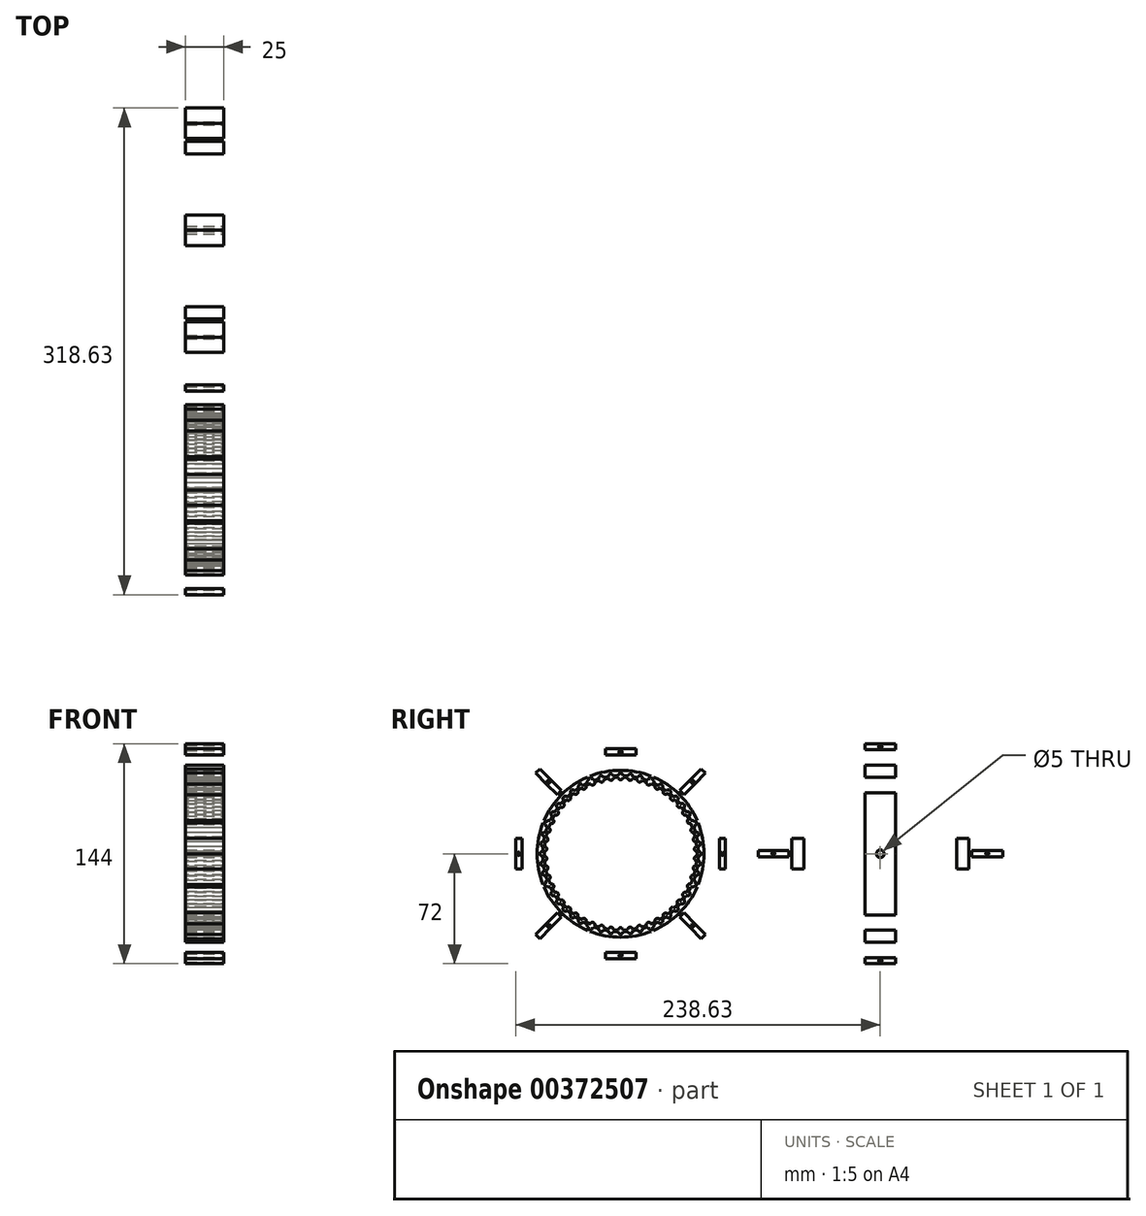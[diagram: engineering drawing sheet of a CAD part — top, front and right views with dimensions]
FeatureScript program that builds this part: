
annotation { "Feature Type Name" : "Feature", "Feature Type Description" : "" }
export const myFeature = defineFeature(function(context is Context, id is Id, definition is map)
    precondition{}
    {
        {
            var Q0;
            Q0=qCreatedBy(makeId("Right.planeOp"),FACE);
            var sketch = newSketch(context, id + "F0", { "sketchPlane" : qUnion([Q0])});
            skLineSegment(sketch, "E0", {"start": v(0, 0) * mm, "end": v(0, 50) * mm, "construction": true});
            skArc(sketch, "E1", {"start": v(3.14, 49.9) * mm, "mid": v(1.57, 49.98) * mm, "end": v(0, 50) * mm});
            skArc(sketch, "E2", {"start": v(-3.14, 49.9) * mm, "mid": v(-1.57, 49.98) * mm, "end": v(0, 50) * mm, "construction": true});
            skArc(sketch, "E3", {"start": v(0, 50) * mm, "mid": v(-1.52, 48.4) * mm, "end": v(-3.14, 49.9) * mm});
            skPoint(sketch, "E3.centerSnap0", {"position": v(-1.57, 49.98) * mm});
            skLineSegment(sketch, "E4", {"start": v(-3.14, 49.9) * mm, "end": v(0, 0) * mm, "construction": true});
            skLineSegment(sketch, "E5", {"start": v(3.14, 49.9) * mm, "end": v(0, 0) * mm, "construction": true});
            skArc(sketch, "E6.1.0", {"start": v(-3.14, 49.9) * mm, "mid": v(-4.7, 49.78) * mm, "end": v(-6.27, 49.6) * mm});
            skArc(sketch, "E6.1.1", {"start": v(-6.27, 49.6) * mm, "mid": v(-7.58, 47.83) * mm, "end": v(-9.37, 49.11) * mm});
            skArc(sketch, "E6.2.0", {"start": v(-9.37, 49.11) * mm, "mid": v(-10.9, 48.8) * mm, "end": v(-12.43, 48.43) * mm});
            skArc(sketch, "E6.2.1", {"start": v(-12.43, 48.43) * mm, "mid": v(-13.51, 46.5) * mm, "end": v(-15.45, 47.55) * mm});
            skArc(sketch, "E7.3.3.0", {"start": v(-15.45, 47.55) * mm, "mid": v(-16.94, 47.04) * mm, "end": v(-18.4, 46.49) * mm});
            skArc(sketch, "E7.4.3.0", {"start": v(-18.4, 46.49) * mm, "mid": v(-19.23, 44.45) * mm, "end": v(-21.29, 45.24) * mm});
            skArc(sketch, "E7.3.4.0", {"start": v(-21.29, 45.24) * mm, "mid": v(-22.7, 44.55) * mm, "end": v(-24.09, 43.82) * mm});
            skArc(sketch, "E7.4.4.0", {"start": v(-24.09, 43.82) * mm, "mid": v(-24.65, 41.69) * mm, "end": v(-26.8, 42.22) * mm});
            skArc(sketch, "E7.3.5.0", {"start": v(-26.8, 42.22) * mm, "mid": v(-28.1, 41.35) * mm, "end": v(-29.39, 40.45) * mm});
            skArc(sketch, "E7.4.5.0", {"start": v(-29.39, 40.45) * mm, "mid": v(-29.68, 38.27) * mm, "end": v(-31.87, 38.53) * mm});
            skArc(sketch, "E7.3.6.0", {"start": v(-31.87, 38.53) * mm, "mid": v(-33.07, 37.5) * mm, "end": v(-34.23, 36.45) * mm});
            skArc(sketch, "E7.4.6.0", {"start": v(-34.23, 36.45) * mm, "mid": v(-34.24, 34.24) * mm, "end": v(-36.45, 34.23) * mm});
            skArc(sketch, "E7.3.7.0", {"start": v(-36.45, 34.23) * mm, "mid": v(-37.5, 33.07) * mm, "end": v(-38.53, 31.87) * mm});
            skArc(sketch, "E7.4.7.0", {"start": v(-38.53, 31.87) * mm, "mid": v(-38.27, 29.68) * mm, "end": v(-40.45, 29.39) * mm});
            skArc(sketch, "E7.3.8.0", {"start": v(-40.45, 29.39) * mm, "mid": v(-41.35, 28.1) * mm, "end": v(-42.22, 26.8) * mm});
            skArc(sketch, "E7.4.8.0", {"start": v(-42.22, 26.8) * mm, "mid": v(-41.69, 24.65) * mm, "end": v(-43.82, 24.09) * mm});
            skArc(sketch, "E7.3.9.0", {"start": v(-43.82, 24.09) * mm, "mid": v(-44.55, 22.7) * mm, "end": v(-45.24, 21.29) * mm});
            skArc(sketch, "E7.4.9.0", {"start": v(-45.24, 21.29) * mm, "mid": v(-44.45, 19.23) * mm, "end": v(-46.49, 18.4) * mm});
            skArc(sketch, "E7.3.10.0", {"start": v(-46.49, 18.4) * mm, "mid": v(-47.04, 16.94) * mm, "end": v(-47.55, 15.45) * mm});
            skArc(sketch, "E7.4.10.0", {"start": v(-47.55, 15.45) * mm, "mid": v(-46.5, 13.51) * mm, "end": v(-48.43, 12.43) * mm});
            skArc(sketch, "E7.3.11.0", {"start": v(-48.43, 12.43) * mm, "mid": v(-48.8, 10.9) * mm, "end": v(-49.11, 9.37) * mm});
            skArc(sketch, "E7.4.11.0", {"start": v(-49.11, 9.37) * mm, "mid": v(-47.83, 7.58) * mm, "end": v(-49.6, 6.27) * mm});
            skArc(sketch, "E7.3.12.0", {"start": v(-49.6, 6.27) * mm, "mid": v(-49.78, 4.7) * mm, "end": v(-49.9, 3.14) * mm});
            skArc(sketch, "E7.4.12.0", {"start": v(-49.9, 3.14) * mm, "mid": v(-48.4, 1.52) * mm, "end": v(-50, 0) * mm});
            skArc(sketch, "E7.3.13.0", {"start": v(-50, 0) * mm, "mid": v(-49.98, -1.57) * mm, "end": v(-49.9, -3.14) * mm});
            skArc(sketch, "E7.4.13.0", {"start": v(-49.9, -3.14) * mm, "mid": v(-48.21, -4.56) * mm, "end": v(-49.6, -6.27) * mm});
            skArc(sketch, "E7.3.14.0", {"start": v(-49.6, -6.27) * mm, "mid": v(-49.38, -7.82) * mm, "end": v(-49.11, -9.37) * mm});
            skArc(sketch, "E7.4.14.0", {"start": v(-49.11, -9.37) * mm, "mid": v(-47.26, -10.56) * mm, "end": v(-48.43, -12.43) * mm});
            skArc(sketch, "E7.3.15.0", {"start": v(-48.43, -12.43) * mm, "mid": v(-48.01, -13.95) * mm, "end": v(-47.55, -15.45) * mm});
            skArc(sketch, "E7.4.15.0", {"start": v(-47.55, -15.45) * mm, "mid": v(-45.57, -16.4) * mm, "end": v(-46.49, -18.4) * mm});
            skArc(sketch, "E7.3.16.0", {"start": v(-46.49, -18.4) * mm, "mid": v(-45.89, -19.86) * mm, "end": v(-45.24, -21.29) * mm});
            skArc(sketch, "E7.4.16.0", {"start": v(-45.24, -21.29) * mm, "mid": v(-43.15, -21.99) * mm, "end": v(-43.82, -24.09) * mm});
            skArc(sketch, "E7.3.17.0", {"start": v(-43.82, -24.09) * mm, "mid": v(-43.04, -25.45) * mm, "end": v(-42.22, -26.8) * mm});
            skArc(sketch, "E7.4.17.0", {"start": v(-42.22, -26.8) * mm, "mid": v(-40.05, -27.22) * mm, "end": v(-40.45, -29.39) * mm});
            skArc(sketch, "E7.3.18.0", {"start": v(-40.45, -29.39) * mm, "mid": v(-39.5, -30.65) * mm, "end": v(-38.53, -31.87) * mm});
            skArc(sketch, "E7.4.18.0", {"start": v(-38.53, -31.87) * mm, "mid": v(-36.33, -32.03) * mm, "end": v(-36.45, -34.23) * mm});
            skArc(sketch, "E7.3.19.0", {"start": v(-36.45, -34.23) * mm, "mid": v(-35.36, -35.36) * mm, "end": v(-34.23, -36.45) * mm});
            skArc(sketch, "E7.4.19.0", {"start": v(-34.23, -36.45) * mm, "mid": v(-32.03, -36.33) * mm, "end": v(-31.87, -38.53) * mm});
            skArc(sketch, "E7.3.20.0", {"start": v(-31.87, -38.53) * mm, "mid": v(-30.65, -39.5) * mm, "end": v(-29.39, -40.45) * mm});
            skArc(sketch, "E7.4.20.0", {"start": v(-29.39, -40.45) * mm, "mid": v(-27.22, -40.05) * mm, "end": v(-26.8, -42.22) * mm});
            skArc(sketch, "E7.3.21.0", {"start": v(-26.8, -42.22) * mm, "mid": v(-25.45, -43.04) * mm, "end": v(-24.09, -43.82) * mm});
            skArc(sketch, "E7.4.21.0", {"start": v(-24.09, -43.82) * mm, "mid": v(-21.99, -43.15) * mm, "end": v(-21.29, -45.24) * mm});
            skArc(sketch, "E7.3.22.0", {"start": v(-21.29, -45.24) * mm, "mid": v(-19.86, -45.89) * mm, "end": v(-18.4, -46.49) * mm});
            skArc(sketch, "E7.4.22.0", {"start": v(-18.4, -46.49) * mm, "mid": v(-16.4, -45.57) * mm, "end": v(-15.45, -47.55) * mm});
            skArc(sketch, "E7.3.23.0", {"start": v(-15.45, -47.55) * mm, "mid": v(-13.95, -48.01) * mm, "end": v(-12.43, -48.43) * mm});
            skArc(sketch, "E7.4.23.0", {"start": v(-12.43, -48.43) * mm, "mid": v(-10.56, -47.26) * mm, "end": v(-9.37, -49.11) * mm});
            skArc(sketch, "E7.3.24.0", {"start": v(-9.37, -49.11) * mm, "mid": v(-7.82, -49.38) * mm, "end": v(-6.27, -49.6) * mm});
            skArc(sketch, "E7.4.24.0", {"start": v(-6.27, -49.6) * mm, "mid": v(-4.56, -48.21) * mm, "end": v(-3.14, -49.9) * mm});
            skArc(sketch, "E7.3.25.0", {"start": v(-3.14, -49.9) * mm, "mid": v(-1.57, -49.98) * mm, "end": v(0, -50) * mm});
            skArc(sketch, "E7.4.25.0", {"start": v(0, -50) * mm, "mid": v(1.52, -48.4) * mm, "end": v(3.14, -49.9) * mm});
            skArc(sketch, "E7.3.26.0", {"start": v(3.14, -49.9) * mm, "mid": v(4.7, -49.78) * mm, "end": v(6.27, -49.6) * mm});
            skArc(sketch, "E7.4.26.0", {"start": v(6.27, -49.6) * mm, "mid": v(7.58, -47.83) * mm, "end": v(9.37, -49.11) * mm});
            skArc(sketch, "E7.3.27.0", {"start": v(9.37, -49.11) * mm, "mid": v(10.9, -48.8) * mm, "end": v(12.43, -48.43) * mm});
            skArc(sketch, "E7.4.27.0", {"start": v(12.43, -48.43) * mm, "mid": v(13.51, -46.5) * mm, "end": v(15.45, -47.55) * mm});
            skArc(sketch, "E7.3.28.0", {"start": v(15.45, -47.55) * mm, "mid": v(16.94, -47.04) * mm, "end": v(18.4, -46.49) * mm});
            skArc(sketch, "E7.4.28.0", {"start": v(18.4, -46.49) * mm, "mid": v(19.23, -44.45) * mm, "end": v(21.29, -45.24) * mm});
            skArc(sketch, "E7.3.29.0", {"start": v(21.29, -45.24) * mm, "mid": v(22.7, -44.55) * mm, "end": v(24.09, -43.82) * mm});
            skArc(sketch, "E7.4.29.0", {"start": v(24.09, -43.82) * mm, "mid": v(24.65, -41.69) * mm, "end": v(26.8, -42.22) * mm});
            skArc(sketch, "E7.3.30.0", {"start": v(26.8, -42.22) * mm, "mid": v(28.1, -41.35) * mm, "end": v(29.39, -40.45) * mm});
            skArc(sketch, "E7.4.30.0", {"start": v(29.39, -40.45) * mm, "mid": v(29.68, -38.27) * mm, "end": v(31.87, -38.53) * mm});
            skArc(sketch, "E7.3.31.0", {"start": v(31.87, -38.53) * mm, "mid": v(33.07, -37.5) * mm, "end": v(34.23, -36.45) * mm});
            skArc(sketch, "E7.4.31.0", {"start": v(34.23, -36.45) * mm, "mid": v(34.24, -34.24) * mm, "end": v(36.45, -34.23) * mm});
            skArc(sketch, "E7.3.32.0", {"start": v(36.45, -34.23) * mm, "mid": v(37.5, -33.07) * mm, "end": v(38.53, -31.87) * mm});
            skArc(sketch, "E7.4.32.0", {"start": v(38.53, -31.87) * mm, "mid": v(38.27, -29.68) * mm, "end": v(40.45, -29.39) * mm});
            skArc(sketch, "E7.3.33.0", {"start": v(40.45, -29.39) * mm, "mid": v(41.35, -28.1) * mm, "end": v(42.22, -26.8) * mm});
            skArc(sketch, "E7.4.33.0", {"start": v(42.22, -26.8) * mm, "mid": v(41.69, -24.65) * mm, "end": v(43.82, -24.09) * mm});
            skArc(sketch, "E7.3.34.0", {"start": v(43.82, -24.09) * mm, "mid": v(44.55, -22.7) * mm, "end": v(45.24, -21.29) * mm});
            skArc(sketch, "E7.4.34.0", {"start": v(45.24, -21.29) * mm, "mid": v(44.45, -19.23) * mm, "end": v(46.49, -18.4) * mm});
            skArc(sketch, "E7.3.35.0", {"start": v(46.49, -18.4) * mm, "mid": v(47.04, -16.94) * mm, "end": v(47.55, -15.45) * mm});
            skArc(sketch, "E7.4.35.0", {"start": v(47.55, -15.45) * mm, "mid": v(46.5, -13.51) * mm, "end": v(48.43, -12.43) * mm});
            skArc(sketch, "E7.3.36.0", {"start": v(48.43, -12.43) * mm, "mid": v(48.8, -10.9) * mm, "end": v(49.11, -9.37) * mm});
            skArc(sketch, "E7.4.36.0", {"start": v(49.11, -9.37) * mm, "mid": v(47.83, -7.58) * mm, "end": v(49.6, -6.27) * mm});
            skArc(sketch, "E7.3.37.0", {"start": v(49.6, -6.27) * mm, "mid": v(49.78, -4.7) * mm, "end": v(49.9, -3.14) * mm});
            skArc(sketch, "E7.4.37.0", {"start": v(49.9, -3.14) * mm, "mid": v(48.4, -1.52) * mm, "end": v(50, 0) * mm});
            skArc(sketch, "E7.3.38.0", {"start": v(50, 0) * mm, "mid": v(49.98, 1.57) * mm, "end": v(49.9, 3.14) * mm});
            skArc(sketch, "E7.4.38.0", {"start": v(49.9, 3.14) * mm, "mid": v(48.21, 4.56) * mm, "end": v(49.6, 6.27) * mm});
            skArc(sketch, "E7.3.39.0", {"start": v(49.6, 6.27) * mm, "mid": v(49.38, 7.82) * mm, "end": v(49.11, 9.37) * mm});
            skArc(sketch, "E7.4.39.0", {"start": v(49.11, 9.37) * mm, "mid": v(47.26, 10.56) * mm, "end": v(48.43, 12.43) * mm});
            skArc(sketch, "E7.3.40.0", {"start": v(48.43, 12.43) * mm, "mid": v(48.01, 13.95) * mm, "end": v(47.55, 15.45) * mm});
            skArc(sketch, "E7.4.40.0", {"start": v(47.55, 15.45) * mm, "mid": v(45.57, 16.4) * mm, "end": v(46.49, 18.4) * mm});
            skArc(sketch, "E7.3.41.0", {"start": v(46.49, 18.4) * mm, "mid": v(45.89, 19.86) * mm, "end": v(45.24, 21.29) * mm});
            skArc(sketch, "E7.4.41.0", {"start": v(45.24, 21.29) * mm, "mid": v(43.15, 21.99) * mm, "end": v(43.82, 24.09) * mm});
            skArc(sketch, "E7.3.42.0", {"start": v(43.82, 24.09) * mm, "mid": v(43.04, 25.45) * mm, "end": v(42.22, 26.8) * mm});
            skArc(sketch, "E7.4.42.0", {"start": v(42.22, 26.8) * mm, "mid": v(40.05, 27.22) * mm, "end": v(40.45, 29.39) * mm});
            skArc(sketch, "E7.3.43.0", {"start": v(40.45, 29.39) * mm, "mid": v(39.5, 30.65) * mm, "end": v(38.53, 31.87) * mm});
            skArc(sketch, "E7.4.43.0", {"start": v(38.53, 31.87) * mm, "mid": v(36.33, 32.03) * mm, "end": v(36.45, 34.23) * mm});
            skArc(sketch, "E7.3.44.0", {"start": v(36.45, 34.23) * mm, "mid": v(35.36, 35.36) * mm, "end": v(34.23, 36.45) * mm});
            skArc(sketch, "E7.4.44.0", {"start": v(34.23, 36.45) * mm, "mid": v(32.03, 36.33) * mm, "end": v(31.87, 38.53) * mm});
            skArc(sketch, "E7.3.45.0", {"start": v(31.87, 38.53) * mm, "mid": v(30.65, 39.5) * mm, "end": v(29.39, 40.45) * mm});
            skArc(sketch, "E7.4.45.0", {"start": v(29.39, 40.45) * mm, "mid": v(27.22, 40.05) * mm, "end": v(26.8, 42.22) * mm});
            skArc(sketch, "E7.3.46.0", {"start": v(26.8, 42.22) * mm, "mid": v(25.45, 43.04) * mm, "end": v(24.09, 43.82) * mm});
            skArc(sketch, "E7.4.46.0", {"start": v(24.09, 43.82) * mm, "mid": v(21.99, 43.15) * mm, "end": v(21.29, 45.24) * mm});
            skArc(sketch, "E7.3.47.0", {"start": v(21.29, 45.24) * mm, "mid": v(19.86, 45.89) * mm, "end": v(18.4, 46.49) * mm});
            skArc(sketch, "E7.4.47.0", {"start": v(18.4, 46.49) * mm, "mid": v(16.4, 45.57) * mm, "end": v(15.45, 47.55) * mm});
            skArc(sketch, "E7.3.48.0", {"start": v(15.45, 47.55) * mm, "mid": v(13.95, 48.01) * mm, "end": v(12.43, 48.43) * mm});
            skArc(sketch, "E7.4.48.0", {"start": v(12.43, 48.43) * mm, "mid": v(10.56, 47.26) * mm, "end": v(9.37, 49.11) * mm});
            skArc(sketch, "E7.3.49.0", {"start": v(9.37, 49.11) * mm, "mid": v(7.82, 49.38) * mm, "end": v(6.27, 49.6) * mm});
            skArc(sketch, "E7.4.49.0", {"start": v(6.27, 49.6) * mm, "mid": v(4.56, 48.21) * mm, "end": v(3.14, 49.9) * mm});
            skArc(sketch, "E8", {"start": v(0, 50) * mm, "mid": v(1.57, 49.98) * mm, "end": v(3.14, 49.9) * mm, "construction": true});
            skLineSegment(sketch, "E9", {"start": v(0, 25) * mm, "end": v(-1.57, 25) * mm, "construction": true});
            skLineSegment(sketch, "E10", {"start": v(0, 25) * mm, "end": v(1.57, 25) * mm, "construction": true});
            skSolve(sketch);
        }
        {
            var Q0;
            Q0 = qSketchRegion(id + "F0", true);
            extrude(context, id + "F1", {"entities" : qUnion([Q0]), "depth" : 25 * mm});
        }
        {
            var Q0;
            Q0=makeQuery(id+"F1.opExtrude","CAP_FACE",FACE,{"disambiguationData":[OSD([sQuery(id+"F0.wireOp",EDGE,"E1"),sQuery(id+"F0.wireOp",EDGE,"E3"),sQuery(id+"F0.wireOp",EDGE,"E6.1.0"),sQuery(id+"F0.wireOp",EDGE,"E6.1.1"),sQuery(id+"F0.wireOp",EDGE,"E6.2.0"),sQuery(id+"F0.wireOp",EDGE,"E6.2.1"),sQuery(id+"F0.wireOp",EDGE,"E7.3.3.0"),sQuery(id+"F0.wireOp",EDGE,"E7.4.3.0"),sQuery(id+"F0.wireOp",EDGE,"E7.3.4.0"),sQuery(id+"F0.wireOp",EDGE,"E7.4.4.0"),sQuery(id+"F0.wireOp",EDGE,"E7.3.5.0"),sQuery(id+"F0.wireOp",EDGE,"E7.4.5.0"),sQuery(id+"F0.wireOp",EDGE,"E7.3.6.0"),sQuery(id+"F0.wireOp",EDGE,"E7.4.6.0"),sQuery(id+"F0.wireOp",EDGE,"E7.3.7.0"),sQuery(id+"F0.wireOp",EDGE,"E7.4.7.0"),sQuery(id+"F0.wireOp",EDGE,"E7.3.8.0"),sQuery(id+"F0.wireOp",EDGE,"E7.4.8.0"),sQuery(id+"F0.wireOp",EDGE,"E7.3.9.0"),sQuery(id+"F0.wireOp",EDGE,"E7.4.9.0"),sQuery(id+"F0.wireOp",EDGE,"E7.3.10.0"),sQuery(id+"F0.wireOp",EDGE,"E7.4.10.0"),sQuery(id+"F0.wireOp",EDGE,"E7.3.11.0"),sQuery(id+"F0.wireOp",EDGE,"E7.4.11.0"),sQuery(id+"F0.wireOp",EDGE,"E7.3.12.0"),sQuery(id+"F0.wireOp",EDGE,"E7.4.12.0"),sQuery(id+"F0.wireOp",EDGE,"E7.3.13.0"),sQuery(id+"F0.wireOp",EDGE,"E7.4.13.0"),sQuery(id+"F0.wireOp",EDGE,"E7.3.14.0"),sQuery(id+"F0.wireOp",EDGE,"E7.4.14.0"),sQuery(id+"F0.wireOp",EDGE,"E7.3.15.0"),sQuery(id+"F0.wireOp",EDGE,"E7.4.15.0"),sQuery(id+"F0.wireOp",EDGE,"E7.3.16.0"),sQuery(id+"F0.wireOp",EDGE,"E7.4.16.0"),sQuery(id+"F0.wireOp",EDGE,"E7.3.17.0"),sQuery(id+"F0.wireOp",EDGE,"E7.4.17.0"),sQuery(id+"F0.wireOp",EDGE,"E7.3.18.0"),sQuery(id+"F0.wireOp",EDGE,"E7.4.18.0"),sQuery(id+"F0.wireOp",EDGE,"E7.3.19.0"),sQuery(id+"F0.wireOp",EDGE,"E7.4.19.0"),sQuery(id+"F0.wireOp",EDGE,"E7.3.20.0"),sQuery(id+"F0.wireOp",EDGE,"E7.4.20.0"),sQuery(id+"F0.wireOp",EDGE,"E7.3.21.0"),sQuery(id+"F0.wireOp",EDGE,"E7.4.21.0"),sQuery(id+"F0.wireOp",EDGE,"E7.3.22.0"),sQuery(id+"F0.wireOp",EDGE,"E7.4.22.0"),sQuery(id+"F0.wireOp",EDGE,"E7.3.23.0"),sQuery(id+"F0.wireOp",EDGE,"E7.4.23.0"),sQuery(id+"F0.wireOp",EDGE,"E7.3.24.0"),sQuery(id+"F0.wireOp",EDGE,"E7.4.24.0"),sQuery(id+"F0.wireOp",EDGE,"E7.3.25.0"),sQuery(id+"F0.wireOp",EDGE,"E7.4.25.0"),sQuery(id+"F0.wireOp",EDGE,"E7.3.26.0"),sQuery(id+"F0.wireOp",EDGE,"E7.4.26.0"),sQuery(id+"F0.wireOp",EDGE,"E7.3.27.0"),sQuery(id+"F0.wireOp",EDGE,"E7.4.27.0"),sQuery(id+"F0.wireOp",EDGE,"E7.3.28.0"),sQuery(id+"F0.wireOp",EDGE,"E7.4.28.0"),sQuery(id+"F0.wireOp",EDGE,"E7.3.29.0"),sQuery(id+"F0.wireOp",EDGE,"E7.4.29.0"),sQuery(id+"F0.wireOp",EDGE,"E7.3.30.0"),sQuery(id+"F0.wireOp",EDGE,"E7.4.30.0"),sQuery(id+"F0.wireOp",EDGE,"E7.3.31.0"),sQuery(id+"F0.wireOp",EDGE,"E7.4.31.0"),sQuery(id+"F0.wireOp",EDGE,"E7.3.32.0"),sQuery(id+"F0.wireOp",EDGE,"E7.4.32.0"),sQuery(id+"F0.wireOp",EDGE,"E7.3.33.0"),sQuery(id+"F0.wireOp",EDGE,"E7.4.33.0"),sQuery(id+"F0.wireOp",EDGE,"E7.3.34.0"),sQuery(id+"F0.wireOp",EDGE,"E7.4.34.0"),sQuery(id+"F0.wireOp",EDGE,"E7.3.35.0"),sQuery(id+"F0.wireOp",EDGE,"E7.4.35.0"),sQuery(id+"F0.wireOp",EDGE,"E7.3.36.0"),sQuery(id+"F0.wireOp",EDGE,"E7.4.36.0"),sQuery(id+"F0.wireOp",EDGE,"E7.3.37.0"),sQuery(id+"F0.wireOp",EDGE,"E7.4.37.0"),sQuery(id+"F0.wireOp",EDGE,"E7.3.38.0"),sQuery(id+"F0.wireOp",EDGE,"E7.4.38.0"),sQuery(id+"F0.wireOp",EDGE,"E7.3.39.0"),sQuery(id+"F0.wireOp",EDGE,"E7.4.39.0"),sQuery(id+"F0.wireOp",EDGE,"E7.3.40.0"),sQuery(id+"F0.wireOp",EDGE,"E7.4.40.0"),sQuery(id+"F0.wireOp",EDGE,"E7.3.41.0"),sQuery(id+"F0.wireOp",EDGE,"E7.4.41.0"),sQuery(id+"F0.wireOp",EDGE,"E7.3.42.0"),sQuery(id+"F0.wireOp",EDGE,"E7.4.42.0"),sQuery(id+"F0.wireOp",EDGE,"E7.3.43.0"),sQuery(id+"F0.wireOp",EDGE,"E7.4.43.0"),sQuery(id+"F0.wireOp",EDGE,"E7.3.44.0"),sQuery(id+"F0.wireOp",EDGE,"E7.4.44.0"),sQuery(id+"F0.wireOp",EDGE,"E7.3.45.0"),sQuery(id+"F0.wireOp",EDGE,"E7.4.45.0"),sQuery(id+"F0.wireOp",EDGE,"E7.3.46.0"),sQuery(id+"F0.wireOp",EDGE,"E7.4.46.0"),sQuery(id+"F0.wireOp",EDGE,"E7.3.47.0"),sQuery(id+"F0.wireOp",EDGE,"E7.4.47.0"),sQuery(id+"F0.wireOp",EDGE,"E7.3.48.0"),sQuery(id+"F0.wireOp",EDGE,"E7.4.48.0"),sQuery(id+"F0.wireOp",EDGE,"E7.3.49.0"),sQuery(id+"F0.wireOp",EDGE,"E7.4.49.0")])],"isStart":false});
            var sketch = newSketch(context, id + "F2", { "sketchPlane" : qUnion([Q0])});
            skCircle(sketch, "E11", {"center": v(0, 0) * mm, "radius": 56.89 * mm, "construction": true});
            skSolve(sketch);
        }
        {
            var Q0;
            Q0=makeQuery(id+"F1.opExtrude","SWEPT_BODY",BODY,{"disambiguationData":[OSD([sQuery(id+"F0.wireOp",EDGE,"E1"),sQuery(id+"F0.wireOp",EDGE,"E3"),sQuery(id+"F0.wireOp",EDGE,"E6.1.0"),sQuery(id+"F0.wireOp",EDGE,"E6.1.1"),sQuery(id+"F0.wireOp",EDGE,"E6.2.0"),sQuery(id+"F0.wireOp",EDGE,"E6.2.1"),sQuery(id+"F0.wireOp",EDGE,"E7.3.3.0"),sQuery(id+"F0.wireOp",EDGE,"E7.4.3.0"),sQuery(id+"F0.wireOp",EDGE,"E7.3.4.0"),sQuery(id+"F0.wireOp",EDGE,"E7.4.4.0"),sQuery(id+"F0.wireOp",EDGE,"E7.3.5.0"),sQuery(id+"F0.wireOp",EDGE,"E7.4.5.0"),sQuery(id+"F0.wireOp",EDGE,"E7.3.6.0"),sQuery(id+"F0.wireOp",EDGE,"E7.4.6.0"),sQuery(id+"F0.wireOp",EDGE,"E7.3.7.0"),sQuery(id+"F0.wireOp",EDGE,"E7.4.7.0"),sQuery(id+"F0.wireOp",EDGE,"E7.3.8.0"),sQuery(id+"F0.wireOp",EDGE,"E7.4.8.0"),sQuery(id+"F0.wireOp",EDGE,"E7.3.9.0"),sQuery(id+"F0.wireOp",EDGE,"E7.4.9.0"),sQuery(id+"F0.wireOp",EDGE,"E7.3.10.0"),sQuery(id+"F0.wireOp",EDGE,"E7.4.10.0"),sQuery(id+"F0.wireOp",EDGE,"E7.3.11.0"),sQuery(id+"F0.wireOp",EDGE,"E7.4.11.0"),sQuery(id+"F0.wireOp",EDGE,"E7.3.12.0"),sQuery(id+"F0.wireOp",EDGE,"E7.4.12.0"),sQuery(id+"F0.wireOp",EDGE,"E7.3.13.0"),sQuery(id+"F0.wireOp",EDGE,"E7.4.13.0"),sQuery(id+"F0.wireOp",EDGE,"E7.3.14.0"),sQuery(id+"F0.wireOp",EDGE,"E7.4.14.0"),sQuery(id+"F0.wireOp",EDGE,"E7.3.15.0"),sQuery(id+"F0.wireOp",EDGE,"E7.4.15.0"),sQuery(id+"F0.wireOp",EDGE,"E7.3.16.0"),sQuery(id+"F0.wireOp",EDGE,"E7.4.16.0"),sQuery(id+"F0.wireOp",EDGE,"E7.3.17.0"),sQuery(id+"F0.wireOp",EDGE,"E7.4.17.0"),sQuery(id+"F0.wireOp",EDGE,"E7.3.18.0"),sQuery(id+"F0.wireOp",EDGE,"E7.4.18.0"),sQuery(id+"F0.wireOp",EDGE,"E7.3.19.0"),sQuery(id+"F0.wireOp",EDGE,"E7.4.19.0"),sQuery(id+"F0.wireOp",EDGE,"E7.3.20.0"),sQuery(id+"F0.wireOp",EDGE,"E7.4.20.0"),sQuery(id+"F0.wireOp",EDGE,"E7.3.21.0"),sQuery(id+"F0.wireOp",EDGE,"E7.4.21.0"),sQuery(id+"F0.wireOp",EDGE,"E7.3.22.0"),sQuery(id+"F0.wireOp",EDGE,"E7.4.22.0"),sQuery(id+"F0.wireOp",EDGE,"E7.3.23.0"),sQuery(id+"F0.wireOp",EDGE,"E7.4.23.0"),sQuery(id+"F0.wireOp",EDGE,"E7.3.24.0"),sQuery(id+"F0.wireOp",EDGE,"E7.4.24.0"),sQuery(id+"F0.wireOp",EDGE,"E7.3.25.0"),sQuery(id+"F0.wireOp",EDGE,"E7.4.25.0"),sQuery(id+"F0.wireOp",EDGE,"E7.3.26.0"),sQuery(id+"F0.wireOp",EDGE,"E7.4.26.0"),sQuery(id+"F0.wireOp",EDGE,"E7.3.27.0"),sQuery(id+"F0.wireOp",EDGE,"E7.4.27.0"),sQuery(id+"F0.wireOp",EDGE,"E7.3.28.0"),sQuery(id+"F0.wireOp",EDGE,"E7.4.28.0"),sQuery(id+"F0.wireOp",EDGE,"E7.3.29.0"),sQuery(id+"F0.wireOp",EDGE,"E7.4.29.0"),sQuery(id+"F0.wireOp",EDGE,"E7.3.30.0"),sQuery(id+"F0.wireOp",EDGE,"E7.4.30.0"),sQuery(id+"F0.wireOp",EDGE,"E7.3.31.0"),sQuery(id+"F0.wireOp",EDGE,"E7.4.31.0"),sQuery(id+"F0.wireOp",EDGE,"E7.3.32.0"),sQuery(id+"F0.wireOp",EDGE,"E7.4.32.0"),sQuery(id+"F0.wireOp",EDGE,"E7.3.33.0"),sQuery(id+"F0.wireOp",EDGE,"E7.4.33.0"),sQuery(id+"F0.wireOp",EDGE,"E7.3.34.0"),sQuery(id+"F0.wireOp",EDGE,"E7.4.34.0"),sQuery(id+"F0.wireOp",EDGE,"E7.3.35.0"),sQuery(id+"F0.wireOp",EDGE,"E7.4.35.0"),sQuery(id+"F0.wireOp",EDGE,"E7.3.36.0"),sQuery(id+"F0.wireOp",EDGE,"E7.4.36.0"),sQuery(id+"F0.wireOp",EDGE,"E7.3.37.0"),sQuery(id+"F0.wireOp",EDGE,"E7.4.37.0"),sQuery(id+"F0.wireOp",EDGE,"E7.3.38.0"),sQuery(id+"F0.wireOp",EDGE,"E7.4.38.0"),sQuery(id+"F0.wireOp",EDGE,"E7.3.39.0"),sQuery(id+"F0.wireOp",EDGE,"E7.4.39.0"),sQuery(id+"F0.wireOp",EDGE,"E7.3.40.0"),sQuery(id+"F0.wireOp",EDGE,"E7.4.40.0"),sQuery(id+"F0.wireOp",EDGE,"E7.3.41.0"),sQuery(id+"F0.wireOp",EDGE,"E7.4.41.0"),sQuery(id+"F0.wireOp",EDGE,"E7.3.42.0"),sQuery(id+"F0.wireOp",EDGE,"E7.4.42.0"),sQuery(id+"F0.wireOp",EDGE,"E7.3.43.0"),sQuery(id+"F0.wireOp",EDGE,"E7.4.43.0"),sQuery(id+"F0.wireOp",EDGE,"E7.3.44.0"),sQuery(id+"F0.wireOp",EDGE,"E7.4.44.0"),sQuery(id+"F0.wireOp",EDGE,"E7.3.45.0"),sQuery(id+"F0.wireOp",EDGE,"E7.4.45.0"),sQuery(id+"F0.wireOp",EDGE,"E7.3.46.0"),sQuery(id+"F0.wireOp",EDGE,"E7.4.46.0"),sQuery(id+"F0.wireOp",EDGE,"E7.3.47.0"),sQuery(id+"F0.wireOp",EDGE,"E7.4.47.0"),sQuery(id+"F0.wireOp",EDGE,"E7.3.48.0"),sQuery(id+"F0.wireOp",EDGE,"E7.4.48.0"),sQuery(id+"F0.wireOp",EDGE,"E7.3.49.0"),sQuery(id+"F0.wireOp",EDGE,"E7.4.49.0")])]});
            var Q1;
            Q1=sQuery(id+"F2.wireOp",EDGE,"E11");
            transform(context, id + "F3", {"entities" : qUnion([Q0]), "transformType" : TransformType.ROTATION, "transformAxis" : qUnion([Q1]), "angle" : 1.8 * degree, "makeCopy" : false});
        }
        {
            var Q0;
            Q0=makeQuery(id+"F1.opExtrude","CAP_FACE",FACE,{"disambiguationData":[OSD([sQuery(id+"F0.wireOp",EDGE,"E1"),sQuery(id+"F0.wireOp",EDGE,"E3"),sQuery(id+"F0.wireOp",EDGE,"E6.1.0"),sQuery(id+"F0.wireOp",EDGE,"E6.1.1"),sQuery(id+"F0.wireOp",EDGE,"E6.2.0"),sQuery(id+"F0.wireOp",EDGE,"E6.2.1"),sQuery(id+"F0.wireOp",EDGE,"E7.3.3.0"),sQuery(id+"F0.wireOp",EDGE,"E7.4.3.0"),sQuery(id+"F0.wireOp",EDGE,"E7.3.4.0"),sQuery(id+"F0.wireOp",EDGE,"E7.4.4.0"),sQuery(id+"F0.wireOp",EDGE,"E7.3.5.0"),sQuery(id+"F0.wireOp",EDGE,"E7.4.5.0"),sQuery(id+"F0.wireOp",EDGE,"E7.3.6.0"),sQuery(id+"F0.wireOp",EDGE,"E7.4.6.0"),sQuery(id+"F0.wireOp",EDGE,"E7.3.7.0"),sQuery(id+"F0.wireOp",EDGE,"E7.4.7.0"),sQuery(id+"F0.wireOp",EDGE,"E7.3.8.0"),sQuery(id+"F0.wireOp",EDGE,"E7.4.8.0"),sQuery(id+"F0.wireOp",EDGE,"E7.3.9.0"),sQuery(id+"F0.wireOp",EDGE,"E7.4.9.0"),sQuery(id+"F0.wireOp",EDGE,"E7.3.10.0"),sQuery(id+"F0.wireOp",EDGE,"E7.4.10.0"),sQuery(id+"F0.wireOp",EDGE,"E7.3.11.0"),sQuery(id+"F0.wireOp",EDGE,"E7.4.11.0"),sQuery(id+"F0.wireOp",EDGE,"E7.3.12.0"),sQuery(id+"F0.wireOp",EDGE,"E7.4.12.0"),sQuery(id+"F0.wireOp",EDGE,"E7.3.13.0"),sQuery(id+"F0.wireOp",EDGE,"E7.4.13.0"),sQuery(id+"F0.wireOp",EDGE,"E7.3.14.0"),sQuery(id+"F0.wireOp",EDGE,"E7.4.14.0"),sQuery(id+"F0.wireOp",EDGE,"E7.3.15.0"),sQuery(id+"F0.wireOp",EDGE,"E7.4.15.0"),sQuery(id+"F0.wireOp",EDGE,"E7.3.16.0"),sQuery(id+"F0.wireOp",EDGE,"E7.4.16.0"),sQuery(id+"F0.wireOp",EDGE,"E7.3.17.0"),sQuery(id+"F0.wireOp",EDGE,"E7.4.17.0"),sQuery(id+"F0.wireOp",EDGE,"E7.3.18.0"),sQuery(id+"F0.wireOp",EDGE,"E7.4.18.0"),sQuery(id+"F0.wireOp",EDGE,"E7.3.19.0"),sQuery(id+"F0.wireOp",EDGE,"E7.4.19.0"),sQuery(id+"F0.wireOp",EDGE,"E7.3.20.0"),sQuery(id+"F0.wireOp",EDGE,"E7.4.20.0"),sQuery(id+"F0.wireOp",EDGE,"E7.3.21.0"),sQuery(id+"F0.wireOp",EDGE,"E7.4.21.0"),sQuery(id+"F0.wireOp",EDGE,"E7.3.22.0"),sQuery(id+"F0.wireOp",EDGE,"E7.4.22.0"),sQuery(id+"F0.wireOp",EDGE,"E7.3.23.0"),sQuery(id+"F0.wireOp",EDGE,"E7.4.23.0"),sQuery(id+"F0.wireOp",EDGE,"E7.3.24.0"),sQuery(id+"F0.wireOp",EDGE,"E7.4.24.0"),sQuery(id+"F0.wireOp",EDGE,"E7.3.25.0"),sQuery(id+"F0.wireOp",EDGE,"E7.4.25.0"),sQuery(id+"F0.wireOp",EDGE,"E7.3.26.0"),sQuery(id+"F0.wireOp",EDGE,"E7.4.26.0"),sQuery(id+"F0.wireOp",EDGE,"E7.3.27.0"),sQuery(id+"F0.wireOp",EDGE,"E7.4.27.0"),sQuery(id+"F0.wireOp",EDGE,"E7.3.28.0"),sQuery(id+"F0.wireOp",EDGE,"E7.4.28.0"),sQuery(id+"F0.wireOp",EDGE,"E7.3.29.0"),sQuery(id+"F0.wireOp",EDGE,"E7.4.29.0"),sQuery(id+"F0.wireOp",EDGE,"E7.3.30.0"),sQuery(id+"F0.wireOp",EDGE,"E7.4.30.0"),sQuery(id+"F0.wireOp",EDGE,"E7.3.31.0"),sQuery(id+"F0.wireOp",EDGE,"E7.4.31.0"),sQuery(id+"F0.wireOp",EDGE,"E7.3.32.0"),sQuery(id+"F0.wireOp",EDGE,"E7.4.32.0"),sQuery(id+"F0.wireOp",EDGE,"E7.3.33.0"),sQuery(id+"F0.wireOp",EDGE,"E7.4.33.0"),sQuery(id+"F0.wireOp",EDGE,"E7.3.34.0"),sQuery(id+"F0.wireOp",EDGE,"E7.4.34.0"),sQuery(id+"F0.wireOp",EDGE,"E7.3.35.0"),sQuery(id+"F0.wireOp",EDGE,"E7.4.35.0"),sQuery(id+"F0.wireOp",EDGE,"E7.3.36.0"),sQuery(id+"F0.wireOp",EDGE,"E7.4.36.0"),sQuery(id+"F0.wireOp",EDGE,"E7.3.37.0"),sQuery(id+"F0.wireOp",EDGE,"E7.4.37.0"),sQuery(id+"F0.wireOp",EDGE,"E7.3.38.0"),sQuery(id+"F0.wireOp",EDGE,"E7.4.38.0"),sQuery(id+"F0.wireOp",EDGE,"E7.3.39.0"),sQuery(id+"F0.wireOp",EDGE,"E7.4.39.0"),sQuery(id+"F0.wireOp",EDGE,"E7.3.40.0"),sQuery(id+"F0.wireOp",EDGE,"E7.4.40.0"),sQuery(id+"F0.wireOp",EDGE,"E7.3.41.0"),sQuery(id+"F0.wireOp",EDGE,"E7.4.41.0"),sQuery(id+"F0.wireOp",EDGE,"E7.3.42.0"),sQuery(id+"F0.wireOp",EDGE,"E7.4.42.0"),sQuery(id+"F0.wireOp",EDGE,"E7.3.43.0"),sQuery(id+"F0.wireOp",EDGE,"E7.4.43.0"),sQuery(id+"F0.wireOp",EDGE,"E7.3.44.0"),sQuery(id+"F0.wireOp",EDGE,"E7.4.44.0"),sQuery(id+"F0.wireOp",EDGE,"E7.3.45.0"),sQuery(id+"F0.wireOp",EDGE,"E7.4.45.0"),sQuery(id+"F0.wireOp",EDGE,"E7.3.46.0"),sQuery(id+"F0.wireOp",EDGE,"E7.4.46.0"),sQuery(id+"F0.wireOp",EDGE,"E7.3.47.0"),sQuery(id+"F0.wireOp",EDGE,"E7.4.47.0"),sQuery(id+"F0.wireOp",EDGE,"E7.3.48.0"),sQuery(id+"F0.wireOp",EDGE,"E7.4.48.0"),sQuery(id+"F0.wireOp",EDGE,"E7.3.49.0"),sQuery(id+"F0.wireOp",EDGE,"E7.4.49.0")])],"isStart":false});
            var sketch = newSketch(context, id + "F4", { "sketchPlane" : qUnion([Q0])});
            skLineSegment(sketch, "E12", {"start": v(0, 0) * mm, "end": v(0, 50) * mm, "construction": true});
            skArc(sketch, "E13", {"start": v(-1.6, 50.97) * mm, "mid": v(0, 51) * mm, "end": v(1.6, 50.97) * mm});
            skLineSegment(sketch, "E14", {"start": v(0, 0) * mm, "end": v(-1.6, 50.97) * mm, "construction": true});
            skLineSegment(sketch, "E15", {"start": v(1.6, 50.97) * mm, "end": v(0, 0) * mm, "construction": true});
            skLineSegment(sketch, "E16", {"start": v(0, 50) * mm, "end": v(0, 51) * mm, "construction": true});
            skArc(sketch, "E17", {"start": v(-1.6, 50.97) * mm, "mid": v(-2.13, 52.1) * mm, "end": v(-3.3, 52.52) * mm});
            skLineSegment(sketch, "E18", {"start": v(-3.3, 52.52) * mm, "end": v(0, 0) * mm, "construction": true});
            skArc(sketch, "E19.MirrorCS", {"start": v(1.6, 50.97) * mm, "mid": v(2.13, 52.1) * mm, "end": v(3.3, 52.52) * mm});
            skArc(sketch, "E20.1.0", {"start": v(7.98, 50.37) * mm, "mid": v(8.64, 51.43) * mm, "end": v(9.86, 51.7) * mm});
            skArc(sketch, "E20.1.1", {"start": v(4.8, 50.77) * mm, "mid": v(6.4, 50.6) * mm, "end": v(7.98, 50.37) * mm});
            skArc(sketch, "E20.1.2", {"start": v(4.8, 50.77) * mm, "mid": v(4.42, 51.97) * mm, "end": v(3.3, 52.52) * mm});
            skArc(sketch, "E20.2.0", {"start": v(14.23, 48.97) * mm, "mid": v(15.02, 49.94) * mm, "end": v(16.26, 50.05) * mm});
            skArc(sketch, "E20.2.1", {"start": v(11.13, 49.77) * mm, "mid": v(12.68, 49.4) * mm, "end": v(14.23, 48.97) * mm});
            skArc(sketch, "E20.2.2", {"start": v(11.13, 49.77) * mm, "mid": v(10.9, 51) * mm, "end": v(9.86, 51.7) * mm});
            skLineSegment(sketch, "E20.anchor1", {"start": v(0, 0) * mm, "end": v(1.6, 50.97) * mm, "construction": true});
            skLineSegment(sketch, "E20.anchor2", {"start": v(0, 0) * mm, "end": v(20.25, 46.8) * mm, "construction": true});
            skArc(sketch, "E21.2.3.0", {"start": v(20.25, 46.8) * mm, "mid": v(21.16, 47.67) * mm, "end": v(22.4, 47.62) * mm});
            skArc(sketch, "E21.4.3.0", {"start": v(17.28, 47.98) * mm, "mid": v(18.77, 47.42) * mm, "end": v(20.25, 46.8) * mm});
            skArc(sketch, "E21.8.3.0", {"start": v(17.28, 47.98) * mm, "mid": v(17.2, 49.23) * mm, "end": v(16.26, 50.05) * mm});
            skArc(sketch, "E22.MirrorCS", {"start": v(-4.8, 50.77) * mm, "mid": v(-4.42, 51.97) * mm, "end": v(-3.3, 52.52) * mm});
            skArc(sketch, "E23.MirrorCS", {"start": v(-4.8, 50.77) * mm, "mid": v(-6.4, 50.6) * mm, "end": v(-7.98, 50.37) * mm});
            skArc(sketch, "E24.MirrorCS", {"start": v(-7.98, 50.37) * mm, "mid": v(-8.64, 51.43) * mm, "end": v(-9.86, 51.7) * mm});
            skArc(sketch, "E25.MirrorCS", {"start": v(-11.13, 49.77) * mm, "mid": v(-10.9, 51) * mm, "end": v(-9.86, 51.7) * mm});
            skArc(sketch, "E26.MirrorCS", {"start": v(-11.13, 49.77) * mm, "mid": v(-12.68, 49.4) * mm, "end": v(-14.23, 48.97) * mm});
            skArc(sketch, "E27.MirrorCS", {"start": v(-14.23, 48.97) * mm, "mid": v(-15.02, 49.94) * mm, "end": v(-16.26, 50.05) * mm});
            skLineSegment(sketch, "E28", {"start": v(0, 0) * mm, "end": v(22.4, 47.62) * mm, "construction": true});
            skLineSegment(sketch, "E29", {"start": v(0, 0) * mm, "end": v(-16.26, 50.05) * mm, "construction": true});
            skLineSegment(sketch, "E30", {"start": v(-16.26, 50.05) * mm, "end": v(-16.88, 51.95) * mm});
            skLineSegment(sketch, "E31", {"start": v(22.4, 47.62) * mm, "end": v(23.26, 49.43) * mm});
            skArc(sketch, "E32", {"start": v(-16.88, 51.95) * mm, "mid": v(3.43, 54.52) * mm, "end": v(23.26, 49.43) * mm});
            skSolve(sketch);
        }
        {
            var Q0;
            Q0 = qSketchRegion(id + "F4", true);
            extrude(context, id + "F5", {"entities" : qUnion([Q0]), "oppositeDirection" : true, "depth" : 25 * mm});
        }
        {
            var Q0;
            Q0=makeQuery(id+"F5.opExtrude","SWEPT_BODY",BODY,{"disambiguationData":[OSD([sQuery(id+"F4.wireOp",EDGE,"E13"),sQuery(id+"F4.wireOp",EDGE,"E17"),sQuery(id+"F4.wireOp",EDGE,"E19.MirrorCS"),sQuery(id+"F4.wireOp",EDGE,"E20.1.0"),sQuery(id+"F4.wireOp",EDGE,"E20.1.1"),sQuery(id+"F4.wireOp",EDGE,"E20.1.2"),sQuery(id+"F4.wireOp",EDGE,"E20.2.0"),sQuery(id+"F4.wireOp",EDGE,"E20.2.1"),sQuery(id+"F4.wireOp",EDGE,"E20.2.2"),sQuery(id+"F4.wireOp",EDGE,"E21.2.3.0"),sQuery(id+"F4.wireOp",EDGE,"E21.4.3.0"),sQuery(id+"F4.wireOp",EDGE,"E21.8.3.0"),sQuery(id+"F4.wireOp",EDGE,"E22.MirrorCS"),sQuery(id+"F4.wireOp",EDGE,"E23.MirrorCS"),sQuery(id+"F4.wireOp",EDGE,"E24.MirrorCS"),sQuery(id+"F4.wireOp",EDGE,"E25.MirrorCS"),sQuery(id+"F4.wireOp",EDGE,"E26.MirrorCS"),sQuery(id+"F4.wireOp",EDGE,"E27.MirrorCS"),sQuery(id+"F4.wireOp",EDGE,"E30"),sQuery(id+"F4.wireOp",EDGE,"E31"),sQuery(id+"F4.wireOp",EDGE,"E32")])]});
            var Q1;
            Q1=sQuery(id+"F2.wireOp",EDGE,"E11");
            circularPattern(context, id + "F6", {"entities" : qUnion([Q0]), "axis" : qUnion([Q1]), "angle" : 360 * degree, "instanceCount" : 8, "oppositeDirection" : true, "equalSpace" : true, "computeTransformsWithoutBuiltin" : true});
        }
        {
            var Q0;
            Q0=makeQuery(id+"F1.opExtrude","CAP_FACE",FACE,{"disambiguationData":[OSD([sQuery(id+"F0.wireOp",EDGE,"E1"),sQuery(id+"F0.wireOp",EDGE,"E3"),sQuery(id+"F0.wireOp",EDGE,"E6.1.0"),sQuery(id+"F0.wireOp",EDGE,"E6.1.1"),sQuery(id+"F0.wireOp",EDGE,"E6.2.0"),sQuery(id+"F0.wireOp",EDGE,"E6.2.1"),sQuery(id+"F0.wireOp",EDGE,"E7.3.3.0"),sQuery(id+"F0.wireOp",EDGE,"E7.4.3.0"),sQuery(id+"F0.wireOp",EDGE,"E7.3.4.0"),sQuery(id+"F0.wireOp",EDGE,"E7.4.4.0"),sQuery(id+"F0.wireOp",EDGE,"E7.3.5.0"),sQuery(id+"F0.wireOp",EDGE,"E7.4.5.0"),sQuery(id+"F0.wireOp",EDGE,"E7.3.6.0"),sQuery(id+"F0.wireOp",EDGE,"E7.4.6.0"),sQuery(id+"F0.wireOp",EDGE,"E7.3.7.0"),sQuery(id+"F0.wireOp",EDGE,"E7.4.7.0"),sQuery(id+"F0.wireOp",EDGE,"E7.3.8.0"),sQuery(id+"F0.wireOp",EDGE,"E7.4.8.0"),sQuery(id+"F0.wireOp",EDGE,"E7.3.9.0"),sQuery(id+"F0.wireOp",EDGE,"E7.4.9.0"),sQuery(id+"F0.wireOp",EDGE,"E7.3.10.0"),sQuery(id+"F0.wireOp",EDGE,"E7.4.10.0"),sQuery(id+"F0.wireOp",EDGE,"E7.3.11.0"),sQuery(id+"F0.wireOp",EDGE,"E7.4.11.0"),sQuery(id+"F0.wireOp",EDGE,"E7.3.12.0"),sQuery(id+"F0.wireOp",EDGE,"E7.4.12.0"),sQuery(id+"F0.wireOp",EDGE,"E7.3.13.0"),sQuery(id+"F0.wireOp",EDGE,"E7.4.13.0"),sQuery(id+"F0.wireOp",EDGE,"E7.3.14.0"),sQuery(id+"F0.wireOp",EDGE,"E7.4.14.0"),sQuery(id+"F0.wireOp",EDGE,"E7.3.15.0"),sQuery(id+"F0.wireOp",EDGE,"E7.4.15.0"),sQuery(id+"F0.wireOp",EDGE,"E7.3.16.0"),sQuery(id+"F0.wireOp",EDGE,"E7.4.16.0"),sQuery(id+"F0.wireOp",EDGE,"E7.3.17.0"),sQuery(id+"F0.wireOp",EDGE,"E7.4.17.0"),sQuery(id+"F0.wireOp",EDGE,"E7.3.18.0"),sQuery(id+"F0.wireOp",EDGE,"E7.4.18.0"),sQuery(id+"F0.wireOp",EDGE,"E7.3.19.0"),sQuery(id+"F0.wireOp",EDGE,"E7.4.19.0"),sQuery(id+"F0.wireOp",EDGE,"E7.3.20.0"),sQuery(id+"F0.wireOp",EDGE,"E7.4.20.0"),sQuery(id+"F0.wireOp",EDGE,"E7.3.21.0"),sQuery(id+"F0.wireOp",EDGE,"E7.4.21.0"),sQuery(id+"F0.wireOp",EDGE,"E7.3.22.0"),sQuery(id+"F0.wireOp",EDGE,"E7.4.22.0"),sQuery(id+"F0.wireOp",EDGE,"E7.3.23.0"),sQuery(id+"F0.wireOp",EDGE,"E7.4.23.0"),sQuery(id+"F0.wireOp",EDGE,"E7.3.24.0"),sQuery(id+"F0.wireOp",EDGE,"E7.4.24.0"),sQuery(id+"F0.wireOp",EDGE,"E7.3.25.0"),sQuery(id+"F0.wireOp",EDGE,"E7.4.25.0"),sQuery(id+"F0.wireOp",EDGE,"E7.3.26.0"),sQuery(id+"F0.wireOp",EDGE,"E7.4.26.0"),sQuery(id+"F0.wireOp",EDGE,"E7.3.27.0"),sQuery(id+"F0.wireOp",EDGE,"E7.4.27.0"),sQuery(id+"F0.wireOp",EDGE,"E7.3.28.0"),sQuery(id+"F0.wireOp",EDGE,"E7.4.28.0"),sQuery(id+"F0.wireOp",EDGE,"E7.3.29.0"),sQuery(id+"F0.wireOp",EDGE,"E7.4.29.0"),sQuery(id+"F0.wireOp",EDGE,"E7.3.30.0"),sQuery(id+"F0.wireOp",EDGE,"E7.4.30.0"),sQuery(id+"F0.wireOp",EDGE,"E7.3.31.0"),sQuery(id+"F0.wireOp",EDGE,"E7.4.31.0"),sQuery(id+"F0.wireOp",EDGE,"E7.3.32.0"),sQuery(id+"F0.wireOp",EDGE,"E7.4.32.0"),sQuery(id+"F0.wireOp",EDGE,"E7.3.33.0"),sQuery(id+"F0.wireOp",EDGE,"E7.4.33.0"),sQuery(id+"F0.wireOp",EDGE,"E7.3.34.0"),sQuery(id+"F0.wireOp",EDGE,"E7.4.34.0"),sQuery(id+"F0.wireOp",EDGE,"E7.3.35.0"),sQuery(id+"F0.wireOp",EDGE,"E7.4.35.0"),sQuery(id+"F0.wireOp",EDGE,"E7.3.36.0"),sQuery(id+"F0.wireOp",EDGE,"E7.4.36.0"),sQuery(id+"F0.wireOp",EDGE,"E7.3.37.0"),sQuery(id+"F0.wireOp",EDGE,"E7.4.37.0"),sQuery(id+"F0.wireOp",EDGE,"E7.3.38.0"),sQuery(id+"F0.wireOp",EDGE,"E7.4.38.0"),sQuery(id+"F0.wireOp",EDGE,"E7.3.39.0"),sQuery(id+"F0.wireOp",EDGE,"E7.4.39.0"),sQuery(id+"F0.wireOp",EDGE,"E7.3.40.0"),sQuery(id+"F0.wireOp",EDGE,"E7.4.40.0"),sQuery(id+"F0.wireOp",EDGE,"E7.3.41.0"),sQuery(id+"F0.wireOp",EDGE,"E7.4.41.0"),sQuery(id+"F0.wireOp",EDGE,"E7.3.42.0"),sQuery(id+"F0.wireOp",EDGE,"E7.4.42.0"),sQuery(id+"F0.wireOp",EDGE,"E7.3.43.0"),sQuery(id+"F0.wireOp",EDGE,"E7.4.43.0"),sQuery(id+"F0.wireOp",EDGE,"E7.3.44.0"),sQuery(id+"F0.wireOp",EDGE,"E7.4.44.0"),sQuery(id+"F0.wireOp",EDGE,"E7.3.45.0"),sQuery(id+"F0.wireOp",EDGE,"E7.4.45.0"),sQuery(id+"F0.wireOp",EDGE,"E7.3.46.0"),sQuery(id+"F0.wireOp",EDGE,"E7.4.46.0"),sQuery(id+"F0.wireOp",EDGE,"E7.3.47.0"),sQuery(id+"F0.wireOp",EDGE,"E7.4.47.0"),sQuery(id+"F0.wireOp",EDGE,"E7.3.48.0"),sQuery(id+"F0.wireOp",EDGE,"E7.4.48.0"),sQuery(id+"F0.wireOp",EDGE,"E7.3.49.0"),sQuery(id+"F0.wireOp",EDGE,"E7.4.49.0")])],"isStart":false});
            var sketch = newSketch(context, id + "F7", { "sketchPlane" : qUnion([Q0])});
            skLineSegment(sketch, "E33.bottom", {"start": v(160, 40) * mm, "end": v(180, 40) * mm});
            skLineSegment(sketch, "E33.top", {"start": v(160, -40) * mm, "end": v(180, -40) * mm});
            skLineSegment(sketch, "E33.left", {"start": v(160, 40) * mm, "end": v(160, -40) * mm});
            skLineSegment(sketch, "E33.right", {"start": v(180, 40) * mm, "end": v(180, -40) * mm});
            skLineSegment(sketch, "E34", {"start": v(0, 0) * mm, "end": v(160, 0) * mm, "construction": true});
            skLineSegment(sketch, "E35.bottom", {"start": v(160, 58) * mm, "end": v(180, 58) * mm});
            skLineSegment(sketch, "E35.top", {"start": v(160, 50) * mm, "end": v(180, 50) * mm});
            skLineSegment(sketch, "E35.left", {"start": v(160, 58) * mm, "end": v(160, 50) * mm});
            skLineSegment(sketch, "E35.right", {"start": v(180, 58) * mm, "end": v(180, 50) * mm});
            skLineSegment(sketch, "E36.bottom", {"start": v(112, 10) * mm, "end": v(120, 10) * mm});
            skLineSegment(sketch, "E36.top", {"start": v(112, -10) * mm, "end": v(120, -10) * mm});
            skLineSegment(sketch, "E36.left", {"start": v(112, 10) * mm, "end": v(112, -10) * mm});
            skLineSegment(sketch, "E36.right", {"start": v(120, 10) * mm, "end": v(120, -10) * mm});
            skCircle(sketch, "E37", {"center": v(170, 0) * mm, "radius": 50 * mm, "construction": true});
            skPoint(sketch, "E37.centerSnap0", {"position": v(180, 0) * mm});
            skLineSegment(sketch, "E38", {"start": v(170, 0) * mm, "end": v(170, 40) * mm, "construction": true});
            skPoint(sketch, "E39", {"position": v(112, 0) * mm});
            skLineSegment(sketch, "E40.MirrorCS", {"start": v(160, -50) * mm, "end": v(180, -50) * mm});
            skLineSegment(sketch, "E41.MirrorCS", {"start": v(180, -58) * mm, "end": v(180, -50) * mm});
            skLineSegment(sketch, "E42.MirrorCS", {"start": v(160, -58) * mm, "end": v(180, -58) * mm});
            skLineSegment(sketch, "E43.MirrorCS", {"start": v(160, -58) * mm, "end": v(160, -50) * mm});
            skLineSegment(sketch, "E44.MirrorCS", {"start": v(228, 10) * mm, "end": v(220, 10) * mm});
            skLineSegment(sketch, "E45.MirrorCS", {"start": v(228, -10) * mm, "end": v(220, -10) * mm});
            skPoint(sketch, "E46.MirrorP", {"position": v(228, 0) * mm});
            skLineSegment(sketch, "E47.MirrorCS", {"start": v(228, 10) * mm, "end": v(228, -10) * mm});
            skLineSegment(sketch, "E48.MirrorCS", {"start": v(220, 10) * mm, "end": v(220, -10) * mm});
            skCircle(sketch, "E49", {"center": v(170, 0) * mm, "radius": 2.5 * mm});
            skSolve(sketch);
        }
        {
            var Q0;
            Q0 = qSketchRegion(id + "F7", true);
            extrude(context, id + "F8", {"entities" : qUnion([Q0]), "oppositeDirection" : true, "depth" : 25 * mm});
        }
        {
            var Q0;
            Q0=makeQuery(id+"F8.opExtrude","CAP_FACE",FACE,{"disambiguationData":[OSD([sQuery(id+"F7.wireOp",EDGE,"E33.bottom"),sQuery(id+"F7.wireOp",EDGE,"E33.top"),sQuery(id+"F7.wireOp",EDGE,"E33.left"),sQuery(id+"F7.wireOp",EDGE,"E33.right"),sQuery(id+"F7.wireOp",EDGE,"E49")])],"isStart":true});
            var sketch = newSketch(context, id + "F9", { "sketchPlane" : qUnion([Q0])});
            skCircle(sketch, "E50.0", {"center": v(170, 0) * mm, "radius": 2.5 * mm});
            skSolve(sketch);
        }
        {
            var Q0;
            Q0 = qSketchRegion(id + "F9", true);
            extrude(context, id + "F10", {"entities" : qUnion([Q0]), "oppositeDirection" : true, "depth" : 25 * mm});
        }
        {
            var Q0;
            Q0=makeQuery(id+"F1.opExtrude","CAP_FACE",FACE,{"disambiguationData":[OSD([sQuery(id+"F0.wireOp",EDGE,"E1"),sQuery(id+"F0.wireOp",EDGE,"E3"),sQuery(id+"F0.wireOp",EDGE,"E6.1.0"),sQuery(id+"F0.wireOp",EDGE,"E6.1.1"),sQuery(id+"F0.wireOp",EDGE,"E6.2.0"),sQuery(id+"F0.wireOp",EDGE,"E6.2.1"),sQuery(id+"F0.wireOp",EDGE,"E7.3.3.0"),sQuery(id+"F0.wireOp",EDGE,"E7.4.3.0"),sQuery(id+"F0.wireOp",EDGE,"E7.3.4.0"),sQuery(id+"F0.wireOp",EDGE,"E7.4.4.0"),sQuery(id+"F0.wireOp",EDGE,"E7.3.5.0"),sQuery(id+"F0.wireOp",EDGE,"E7.4.5.0"),sQuery(id+"F0.wireOp",EDGE,"E7.3.6.0"),sQuery(id+"F0.wireOp",EDGE,"E7.4.6.0"),sQuery(id+"F0.wireOp",EDGE,"E7.3.7.0"),sQuery(id+"F0.wireOp",EDGE,"E7.4.7.0"),sQuery(id+"F0.wireOp",EDGE,"E7.3.8.0"),sQuery(id+"F0.wireOp",EDGE,"E7.4.8.0"),sQuery(id+"F0.wireOp",EDGE,"E7.3.9.0"),sQuery(id+"F0.wireOp",EDGE,"E7.4.9.0"),sQuery(id+"F0.wireOp",EDGE,"E7.3.10.0"),sQuery(id+"F0.wireOp",EDGE,"E7.4.10.0"),sQuery(id+"F0.wireOp",EDGE,"E7.3.11.0"),sQuery(id+"F0.wireOp",EDGE,"E7.4.11.0"),sQuery(id+"F0.wireOp",EDGE,"E7.3.12.0"),sQuery(id+"F0.wireOp",EDGE,"E7.4.12.0"),sQuery(id+"F0.wireOp",EDGE,"E7.3.13.0"),sQuery(id+"F0.wireOp",EDGE,"E7.4.13.0"),sQuery(id+"F0.wireOp",EDGE,"E7.3.14.0"),sQuery(id+"F0.wireOp",EDGE,"E7.4.14.0"),sQuery(id+"F0.wireOp",EDGE,"E7.3.15.0"),sQuery(id+"F0.wireOp",EDGE,"E7.4.15.0"),sQuery(id+"F0.wireOp",EDGE,"E7.3.16.0"),sQuery(id+"F0.wireOp",EDGE,"E7.4.16.0"),sQuery(id+"F0.wireOp",EDGE,"E7.3.17.0"),sQuery(id+"F0.wireOp",EDGE,"E7.4.17.0"),sQuery(id+"F0.wireOp",EDGE,"E7.3.18.0"),sQuery(id+"F0.wireOp",EDGE,"E7.4.18.0"),sQuery(id+"F0.wireOp",EDGE,"E7.3.19.0"),sQuery(id+"F0.wireOp",EDGE,"E7.4.19.0"),sQuery(id+"F0.wireOp",EDGE,"E7.3.20.0"),sQuery(id+"F0.wireOp",EDGE,"E7.4.20.0"),sQuery(id+"F0.wireOp",EDGE,"E7.3.21.0"),sQuery(id+"F0.wireOp",EDGE,"E7.4.21.0"),sQuery(id+"F0.wireOp",EDGE,"E7.3.22.0"),sQuery(id+"F0.wireOp",EDGE,"E7.4.22.0"),sQuery(id+"F0.wireOp",EDGE,"E7.3.23.0"),sQuery(id+"F0.wireOp",EDGE,"E7.4.23.0"),sQuery(id+"F0.wireOp",EDGE,"E7.3.24.0"),sQuery(id+"F0.wireOp",EDGE,"E7.4.24.0"),sQuery(id+"F0.wireOp",EDGE,"E7.3.25.0"),sQuery(id+"F0.wireOp",EDGE,"E7.4.25.0"),sQuery(id+"F0.wireOp",EDGE,"E7.3.26.0"),sQuery(id+"F0.wireOp",EDGE,"E7.4.26.0"),sQuery(id+"F0.wireOp",EDGE,"E7.3.27.0"),sQuery(id+"F0.wireOp",EDGE,"E7.4.27.0"),sQuery(id+"F0.wireOp",EDGE,"E7.3.28.0"),sQuery(id+"F0.wireOp",EDGE,"E7.4.28.0"),sQuery(id+"F0.wireOp",EDGE,"E7.3.29.0"),sQuery(id+"F0.wireOp",EDGE,"E7.4.29.0"),sQuery(id+"F0.wireOp",EDGE,"E7.3.30.0"),sQuery(id+"F0.wireOp",EDGE,"E7.4.30.0"),sQuery(id+"F0.wireOp",EDGE,"E7.3.31.0"),sQuery(id+"F0.wireOp",EDGE,"E7.4.31.0"),sQuery(id+"F0.wireOp",EDGE,"E7.3.32.0"),sQuery(id+"F0.wireOp",EDGE,"E7.4.32.0"),sQuery(id+"F0.wireOp",EDGE,"E7.3.33.0"),sQuery(id+"F0.wireOp",EDGE,"E7.4.33.0"),sQuery(id+"F0.wireOp",EDGE,"E7.3.34.0"),sQuery(id+"F0.wireOp",EDGE,"E7.4.34.0"),sQuery(id+"F0.wireOp",EDGE,"E7.3.35.0"),sQuery(id+"F0.wireOp",EDGE,"E7.4.35.0"),sQuery(id+"F0.wireOp",EDGE,"E7.3.36.0"),sQuery(id+"F0.wireOp",EDGE,"E7.4.36.0"),sQuery(id+"F0.wireOp",EDGE,"E7.3.37.0"),sQuery(id+"F0.wireOp",EDGE,"E7.4.37.0"),sQuery(id+"F0.wireOp",EDGE,"E7.3.38.0"),sQuery(id+"F0.wireOp",EDGE,"E7.4.38.0"),sQuery(id+"F0.wireOp",EDGE,"E7.3.39.0"),sQuery(id+"F0.wireOp",EDGE,"E7.4.39.0"),sQuery(id+"F0.wireOp",EDGE,"E7.3.40.0"),sQuery(id+"F0.wireOp",EDGE,"E7.4.40.0"),sQuery(id+"F0.wireOp",EDGE,"E7.3.41.0"),sQuery(id+"F0.wireOp",EDGE,"E7.4.41.0"),sQuery(id+"F0.wireOp",EDGE,"E7.3.42.0"),sQuery(id+"F0.wireOp",EDGE,"E7.4.42.0"),sQuery(id+"F0.wireOp",EDGE,"E7.3.43.0"),sQuery(id+"F0.wireOp",EDGE,"E7.4.43.0"),sQuery(id+"F0.wireOp",EDGE,"E7.3.44.0"),sQuery(id+"F0.wireOp",EDGE,"E7.4.44.0"),sQuery(id+"F0.wireOp",EDGE,"E7.3.45.0"),sQuery(id+"F0.wireOp",EDGE,"E7.4.45.0"),sQuery(id+"F0.wireOp",EDGE,"E7.3.46.0"),sQuery(id+"F0.wireOp",EDGE,"E7.4.46.0"),sQuery(id+"F0.wireOp",EDGE,"E7.3.47.0"),sQuery(id+"F0.wireOp",EDGE,"E7.4.47.0"),sQuery(id+"F0.wireOp",EDGE,"E7.3.48.0"),sQuery(id+"F0.wireOp",EDGE,"E7.4.48.0"),sQuery(id+"F0.wireOp",EDGE,"E7.3.49.0"),sQuery(id+"F0.wireOp",EDGE,"E7.4.49.0")])],"isStart":false});
            var sketch = newSketch(context, id + "F11", { "sketchPlane" : qUnion([Q0])});
            skLineSegment(sketch, "E51", {"start": v(3.56, 56.52) * mm, "end": v(3.43, 54.52) * mm, "construction": true});
            skLineSegment(sketch, "E52", {"start": v(5.55, 56.4) * mm, "end": v(1.56, 56.64) * mm});
            skLineSegment(sketch, "E53", {"start": v(1.56, 56.64) * mm, "end": v(2.82, 76.6) * mm});
            skLineSegment(sketch, "E54", {"start": v(2.82, 76.6) * mm, "end": v(6.8, 76.35) * mm});
            skLineSegment(sketch, "E55", {"start": v(6.8, 76.35) * mm, "end": v(5.55, 56.4) * mm});
            skLineSegment(sketch, "E56", {"start": v(2.19, 66.62) * mm, "end": v(6.18, 66.37) * mm});
            skCircle(sketch, "E57", {"center": v(4.18, 66.5) * mm, "radius": 1 * mm});
            skSolve(sketch);
        }
        {
            var Q0;
            {var subQ0=sQuery(id+"F11.wireOp",EDGE,"E52");Q0=makeQuery(id+"F11.imprint","IMPRINT",FACE,{"disambiguationData":[TD([[makeQuery(id+"F11.imprint","IMPRINT",EDGE,{"derivedFrom":subQ0}),-1.0]])]});}
            extrude(context, id + "F12", {"entities" : qUnion([Q0]), "oppositeDirection" : true, "depth" : 25 * mm});
        }
        {
            var Q0;
            {var subQ0=sQuery(id+"F11.wireOp",EDGE,"E54");Q0=makeQuery(id+"F11.imprint","IMPRINT",FACE,{"disambiguationData":[TD([[makeQuery(id+"F11.imprint","IMPRINT",EDGE,{"derivedFrom":subQ0}),-1.0]])]});}
            extrude(context, id + "F13", {"entities" : qUnion([Q0]), "oppositeDirection" : true, "depth" : 25 * mm});
        }
        {
            var Q0;
            {var subQ0=sQuery(id+"F11.wireOp",EDGE,"E57");var subQ1=sQuery(id+"F11.wireOp",EDGE,"E56");var subQ2=makeQuery(id+"F11.imprint","INTERSECT",VERTEX,{"disambiguationData":[OD(0.0)],"derivedFrom":[subQ1,subQ0]});Q0=makeQuery(id+"F11.imprint","IMPRINT",FACE,{"disambiguationData":[TD([[makeQuery(id+"F11.imprint","IMPRINT",EDGE,{"disambiguationData":[TD([[subQ2,-1.0]])],"derivedFrom":subQ1}),1.0]])]});}
            var Q1;
            {var subQ0=sQuery(id+"F11.wireOp",EDGE,"E57");var subQ1=sQuery(id+"F11.wireOp",EDGE,"E56");var subQ2=makeQuery(id+"F11.imprint","INTERSECT",VERTEX,{"disambiguationData":[OD(0.0)],"derivedFrom":[subQ1,subQ0]});Q1=makeQuery(id+"F11.imprint","IMPRINT",FACE,{"disambiguationData":[TD([[makeQuery(id+"F11.imprint","IMPRINT",EDGE,{"disambiguationData":[TD([[subQ2,-1.0]])],"derivedFrom":subQ1}),-1.0]])]});}
            extrude(context, id + "F14", {"entities" : qUnion([Q0, Q1]), "oppositeDirection" : true, "depth" : 25 * mm});
        }
        {
            var Q0;
            Q0=makeQuery(id+"F13.opExtrude","SWEPT_BODY",BODY,{"disambiguationData":[OSD([sQuery(id+"F11.wireOp",EDGE,"E53"),sQuery(id+"F11.wireOp",EDGE,"E54"),sQuery(id+"F11.wireOp",EDGE,"E55"),sQuery(id+"F11.wireOp",EDGE,"E56")])]});
            var Q1;
            Q1=makeQuery(id+"F12.opExtrude","SWEPT_BODY",BODY,{"disambiguationData":[OSD([sQuery(id+"F11.wireOp",EDGE,"E52"),sQuery(id+"F11.wireOp",EDGE,"E53"),sQuery(id+"F11.wireOp",EDGE,"E55"),sQuery(id+"F11.wireOp",EDGE,"E56")])]});
            var Q2;
            Q2=makeQuery(id+"F14.opExtrude","SWEPT_BODY",BODY,{"disambiguationData":[OSD([sQuery(id+"F11.wireOp",EDGE,"E57")])]});
            var Q3;
            Q3=sQuery(id+"F2.wireOp",EDGE,"E11");
            circularPattern(context, id + "F15", {"entities" : qUnion([Q0, Q1, Q2]), "axis" : qUnion([Q3]), "angle" : 360 * degree, "instanceCount" : 8, "equalSpace" : true, "computeTransformsWithoutBuiltin" : true});
        }
        {
            var Q0;
            Q0=makeQuery(id+"F8.opExtrude","CAP_FACE",FACE,{"disambiguationData":[OSD([sQuery(id+"F7.wireOp",EDGE,"E35.bottom"),sQuery(id+"F7.wireOp",EDGE,"E35.top"),sQuery(id+"F7.wireOp",EDGE,"E35.left"),sQuery(id+"F7.wireOp",EDGE,"E35.right")])],"isStart":true});
            var sketch = newSketch(context, id + "F16", { "sketchPlane" : qUnion([Q0])});
            skLineSegment(sketch, "E58.bottom", {"start": v(168, 80) * mm, "end": v(172, 80) * mm});
            skLineSegment(sketch, "E58.top", {"start": v(168, 60) * mm, "end": v(172, 60) * mm});
            skLineSegment(sketch, "E58.left", {"start": v(168, 80) * mm, "end": v(168, 60) * mm});
            skLineSegment(sketch, "E58.right", {"start": v(172, 80) * mm, "end": v(172, 60) * mm});
            skLineSegment(sketch, "E59", {"start": v(170, 58) * mm, "end": v(170, 60) * mm, "construction": true});
            skLineSegment(sketch, "E60", {"start": v(168, 70) * mm, "end": v(172, 70) * mm});
            skCircle(sketch, "E61", {"center": v(170, 70) * mm, "radius": 1 * mm});
            skSolve(sketch);
        }
        {
            var Q0;
            {var subQ0=sQuery(id+"F16.wireOp",EDGE,"E58.bottom");Q0=makeQuery(id+"F16.imprint","IMPRINT",FACE,{"disambiguationData":[TD([[makeQuery(id+"F16.imprint","IMPRINT",EDGE,{"derivedFrom":subQ0}),-1.0]])]});}
            extrude(context, id + "F17", {"entities" : qUnion([Q0]), "oppositeDirection" : true, "depth" : 25 * mm});
        }
        {
            var Q0;
            {var subQ0=sQuery(id+"F16.wireOp",EDGE,"E58.top");Q0=makeQuery(id+"F16.imprint","IMPRINT",FACE,{"disambiguationData":[TD([[makeQuery(id+"F16.imprint","IMPRINT",EDGE,{"derivedFrom":subQ0}),1.0]])]});}
            extrude(context, id + "F18", {"entities" : qUnion([Q0]), "oppositeDirection" : true, "depth" : 25 * mm});
        }
        {
            var Q0;
            {var subQ0=sQuery(id+"F16.wireOp",EDGE,"E61");var subQ1=sQuery(id+"F16.wireOp",EDGE,"E60");var subQ2=makeQuery(id+"F16.imprint","INTERSECT",VERTEX,{"disambiguationData":[OD(0.0)],"derivedFrom":[subQ1,subQ0]});Q0=makeQuery(id+"F16.imprint","IMPRINT",FACE,{"disambiguationData":[TD([[makeQuery(id+"F16.imprint","IMPRINT",EDGE,{"disambiguationData":[TD([[subQ2,-1.0]])],"derivedFrom":subQ1}),1.0]])]});}
            var Q1;
            {var subQ0=sQuery(id+"F16.wireOp",EDGE,"E61");var subQ1=sQuery(id+"F16.wireOp",EDGE,"E60");var subQ2=makeQuery(id+"F16.imprint","INTERSECT",VERTEX,{"disambiguationData":[OD(0.0)],"derivedFrom":[subQ1,subQ0]});Q1=makeQuery(id+"F16.imprint","IMPRINT",FACE,{"disambiguationData":[TD([[makeQuery(id+"F16.imprint","IMPRINT",EDGE,{"disambiguationData":[TD([[subQ2,-1.0]])],"derivedFrom":subQ1}),-1.0]])]});}
            extrude(context, id + "F19", {"entities" : qUnion([Q0, Q1]), "oppositeDirection" : true, "depth" : 25 * mm});
        }
        {
            var Q0;
            Q0=makeQuery(id+"F17.opExtrude","SWEPT_BODY",BODY,{"disambiguationData":[OSD([sQuery(id+"F16.wireOp",EDGE,"E58.bottom"),sQuery(id+"F16.wireOp",EDGE,"E58.left"),sQuery(id+"F16.wireOp",EDGE,"E58.right"),sQuery(id+"F16.wireOp",EDGE,"E60"),sQuery(id+"F16.wireOp",EDGE,"E61")])]});
            var Q1;
            Q1=makeQuery(id+"F19.opExtrude","SWEPT_BODY",BODY,{"disambiguationData":[OSD([sQuery(id+"F16.wireOp",EDGE,"E61")])]});
            var Q2;
            Q2=makeQuery(id+"F18.opExtrude","SWEPT_BODY",BODY,{"disambiguationData":[OSD([sQuery(id+"F16.wireOp",EDGE,"E58.top"),sQuery(id+"F16.wireOp",EDGE,"E58.left"),sQuery(id+"F16.wireOp",EDGE,"E58.right"),sQuery(id+"F16.wireOp",EDGE,"E60"),sQuery(id+"F16.wireOp",EDGE,"E61")])]});
            var Q3;
            Q3=makeQuery(id+"F8.opExtrude","CAP_EDGE",EDGE,{"disambiguationData":[OSD([sQuery(id+"F7.wireOp",EDGE,"E49")])],"isStart":true});
            circularPattern(context, id + "F20", {"entities" : qUnion([Q0, Q1, Q2]), "axis" : qUnion([Q3]), "angle" : 360 * degree, "instanceCount" : 4, "equalSpace" : true, "computeTransformsWithoutBuiltin" : true});
        }
        {
            var Q0;
            Q0=makeQuery(id+"F13.opExtrude","SWEPT_BODY",BODY,{"disambiguationData":[OSD([sQuery(id+"F11.wireOp",EDGE,"E53"),sQuery(id+"F11.wireOp",EDGE,"E54"),sQuery(id+"F11.wireOp",EDGE,"E55"),sQuery(id+"F11.wireOp",EDGE,"E56"),sQuery(id+"F11.wireOp",EDGE,"E57")])]});
            var Q1;
            Q1=makeQuery(id+"F12.opExtrude","SWEPT_BODY",BODY,{"disambiguationData":[OSD([sQuery(id+"F11.wireOp",EDGE,"E52"),sQuery(id+"F11.wireOp",EDGE,"E53"),sQuery(id+"F11.wireOp",EDGE,"E55"),sQuery(id+"F11.wireOp",EDGE,"E56"),sQuery(id+"F11.wireOp",EDGE,"E57")])]});
            var Q2;
            Q2=makeQuery(id+"F14.opExtrude","CAP_EDGE",EDGE,{"disambiguationData":[OSD([sQuery(id+"F11.wireOp",EDGE,"E57")])],"isStart":true});
            transform(context, id + "F21", {"entities" : qUnion([Q0, Q1]), "transformType" : TransformType.ROTATION, "transformAxis" : qUnion([Q2]), "angle" : 90 * degree, "makeCopy" : false});
        }
        {
            var Q0;
            Q0=makeQuery(id+"F15.opPattern","COPY",BODY,{"derivedFrom":makeQuery(id+"F13.opExtrude","SWEPT_BODY",BODY,{"disambiguationData":[OSD([sQuery(id+"F11.wireOp",EDGE,"E53"),sQuery(id+"F11.wireOp",EDGE,"E54"),sQuery(id+"F11.wireOp",EDGE,"E55"),sQuery(id+"F11.wireOp",EDGE,"E56"),sQuery(id+"F11.wireOp",EDGE,"E57")])]}),"instanceName":"6"});
            var Q1;
            Q1=makeQuery(id+"F15.opPattern","COPY",BODY,{"derivedFrom":makeQuery(id+"F12.opExtrude","SWEPT_BODY",BODY,{"disambiguationData":[OSD([sQuery(id+"F11.wireOp",EDGE,"E52"),sQuery(id+"F11.wireOp",EDGE,"E53"),sQuery(id+"F11.wireOp",EDGE,"E55"),sQuery(id+"F11.wireOp",EDGE,"E56"),sQuery(id+"F11.wireOp",EDGE,"E57")])]}),"instanceName":"6"});
            var Q2;
            Q2=makeQuery(id+"F15.opPattern","COPY",EDGE,{"derivedFrom":makeQuery(id+"F14.opExtrude","CAP_EDGE",EDGE,{"disambiguationData":[OSD([sQuery(id+"F11.wireOp",EDGE,"E57")])],"isStart":true}),"instanceName":"6"});
            transform(context, id + "F22", {"entities" : qUnion([Q0, Q1]), "transformType" : TransformType.ROTATION, "transformAxis" : qUnion([Q2]), "angle" : 180 * degree, "makeCopy" : false});
        }
        {
            var Q0;
            Q0=makeQuery(id+"F15.opPattern","COPY",BODY,{"derivedFrom":makeQuery(id+"F12.opExtrude","SWEPT_BODY",BODY,{"disambiguationData":[OSD([sQuery(id+"F11.wireOp",EDGE,"E52"),sQuery(id+"F11.wireOp",EDGE,"E53"),sQuery(id+"F11.wireOp",EDGE,"E55"),sQuery(id+"F11.wireOp",EDGE,"E56"),sQuery(id+"F11.wireOp",EDGE,"E57")])]}),"instanceName":"2"});
            var Q1;
            Q1=makeQuery(id+"F15.opPattern","COPY",BODY,{"derivedFrom":makeQuery(id+"F13.opExtrude","SWEPT_BODY",BODY,{"disambiguationData":[OSD([sQuery(id+"F11.wireOp",EDGE,"E53"),sQuery(id+"F11.wireOp",EDGE,"E54"),sQuery(id+"F11.wireOp",EDGE,"E55"),sQuery(id+"F11.wireOp",EDGE,"E56"),sQuery(id+"F11.wireOp",EDGE,"E57")])]}),"instanceName":"2"});
            var Q2;
            Q2=makeQuery(id+"F15.opPattern","COPY",EDGE,{"derivedFrom":makeQuery(id+"F14.opExtrude","CAP_EDGE",EDGE,{"disambiguationData":[OSD([sQuery(id+"F11.wireOp",EDGE,"E57")])],"isStart":true}),"instanceName":"2"});
            transform(context, id + "F23", {"entities" : qUnion([Q0, Q1]), "transformType" : TransformType.ROTATION, "transformAxis" : qUnion([Q2]), "angle" : 180 * degree, "makeCopy" : false});
        }
        {
            var Q0;
            Q0=makeQuery(id+"F15.opPattern","COPY",BODY,{"derivedFrom":makeQuery(id+"F12.opExtrude","SWEPT_BODY",BODY,{"disambiguationData":[OSD([sQuery(id+"F11.wireOp",EDGE,"E52"),sQuery(id+"F11.wireOp",EDGE,"E53"),sQuery(id+"F11.wireOp",EDGE,"E55"),sQuery(id+"F11.wireOp",EDGE,"E56"),sQuery(id+"F11.wireOp",EDGE,"E57")])]}),"instanceName":"4"});
            var Q1;
            Q1=makeQuery(id+"F15.opPattern","COPY",BODY,{"derivedFrom":makeQuery(id+"F13.opExtrude","SWEPT_BODY",BODY,{"disambiguationData":[OSD([sQuery(id+"F11.wireOp",EDGE,"E53"),sQuery(id+"F11.wireOp",EDGE,"E54"),sQuery(id+"F11.wireOp",EDGE,"E55"),sQuery(id+"F11.wireOp",EDGE,"E56"),sQuery(id+"F11.wireOp",EDGE,"E57")])]}),"instanceName":"4"});
            var Q2;
            Q2=makeQuery(id+"F15.opPattern","COPY",EDGE,{"derivedFrom":makeQuery(id+"F14.opExtrude","CAP_EDGE",EDGE,{"disambiguationData":[OSD([sQuery(id+"F11.wireOp",EDGE,"E57")])],"isStart":true}),"instanceName":"4"});
            transform(context, id + "F24", {"entities" : qUnion([Q0, Q1]), "transformType" : TransformType.ROTATION, "transformAxis" : qUnion([Q2]), "angle" : 90 * degree, "makeCopy" : false});
        }
        {
            var Q0;
            Q0=makeQuery(id+"F15.opPattern","COPY",BODY,{"derivedFrom":makeQuery(id+"F12.opExtrude","SWEPT_BODY",BODY,{"disambiguationData":[OSD([sQuery(id+"F11.wireOp",EDGE,"E52"),sQuery(id+"F11.wireOp",EDGE,"E53"),sQuery(id+"F11.wireOp",EDGE,"E55"),sQuery(id+"F11.wireOp",EDGE,"E56"),sQuery(id+"F11.wireOp",EDGE,"E57")])]}),"instanceName":"6"});
            var Q1;
            Q1=makeQuery(id+"F15.opPattern","COPY",BODY,{"derivedFrom":makeQuery(id+"F13.opExtrude","SWEPT_BODY",BODY,{"disambiguationData":[OSD([sQuery(id+"F11.wireOp",EDGE,"E53"),sQuery(id+"F11.wireOp",EDGE,"E54"),sQuery(id+"F11.wireOp",EDGE,"E55"),sQuery(id+"F11.wireOp",EDGE,"E56"),sQuery(id+"F11.wireOp",EDGE,"E57")])]}),"instanceName":"6"});
            var Q2;
            Q2=makeQuery(id+"F15.opPattern","COPY",EDGE,{"derivedFrom":makeQuery(id+"F14.opExtrude","CAP_EDGE",EDGE,{"disambiguationData":[OSD([sQuery(id+"F11.wireOp",EDGE,"E57")])],"isStart":true}),"instanceName":"6"});
            transform(context, id + "F25", {"entities" : qUnion([Q0, Q1]), "transformType" : TransformType.ROTATION, "transformAxis" : qUnion([Q2]), "angle" : 90 * degree, "makeCopy" : false});
        }
        {
            var Q0;
            Q0=makeQuery(id+"F15.opPattern","COPY",BODY,{"derivedFrom":makeQuery(id+"F13.opExtrude","SWEPT_BODY",BODY,{"disambiguationData":[OSD([sQuery(id+"F11.wireOp",EDGE,"E53"),sQuery(id+"F11.wireOp",EDGE,"E54"),sQuery(id+"F11.wireOp",EDGE,"E55"),sQuery(id+"F11.wireOp",EDGE,"E56"),sQuery(id+"F11.wireOp",EDGE,"E57")])]}),"instanceName":"2"});
            var Q1;
            Q1=makeQuery(id+"F15.opPattern","COPY",BODY,{"derivedFrom":makeQuery(id+"F12.opExtrude","SWEPT_BODY",BODY,{"disambiguationData":[OSD([sQuery(id+"F11.wireOp",EDGE,"E52"),sQuery(id+"F11.wireOp",EDGE,"E53"),sQuery(id+"F11.wireOp",EDGE,"E55"),sQuery(id+"F11.wireOp",EDGE,"E56"),sQuery(id+"F11.wireOp",EDGE,"E57")])]}),"instanceName":"2"});
            var Q2;
            Q2=makeQuery(id+"F15.opPattern","COPY",EDGE,{"derivedFrom":makeQuery(id+"F14.opExtrude","CAP_EDGE",EDGE,{"disambiguationData":[OSD([sQuery(id+"F11.wireOp",EDGE,"E57")])],"isStart":true}),"instanceName":"2"});
            transform(context, id + "F26", {"entities" : qUnion([Q0, Q1]), "transformType" : TransformType.ROTATION, "transformAxis" : qUnion([Q2]), "angle" : 90 * degree, "makeCopy" : false});
        }
        {
            var Q0;
            Q0=makeQuery(id+"F15.opPattern","COPY",BODY,{"derivedFrom":makeQuery(id+"F13.opExtrude","SWEPT_BODY",BODY,{"disambiguationData":[OSD([sQuery(id+"F11.wireOp",EDGE,"E53"),sQuery(id+"F11.wireOp",EDGE,"E54"),sQuery(id+"F11.wireOp",EDGE,"E55"),sQuery(id+"F11.wireOp",EDGE,"E56"),sQuery(id+"F11.wireOp",EDGE,"E57")])]}),"instanceName":"4"});
            var Q1;
            Q1=makeQuery(id+"F6.opPattern","COPY",BODY,{"derivedFrom":makeQuery(id+"F5.opExtrude","SWEPT_BODY",BODY,{"disambiguationData":[OSD([sQuery(id+"F4.wireOp",EDGE,"E13"),sQuery(id+"F4.wireOp",EDGE,"E17"),sQuery(id+"F4.wireOp",EDGE,"E19.MirrorCS"),sQuery(id+"F4.wireOp",EDGE,"E20.1.0"),sQuery(id+"F4.wireOp",EDGE,"E20.1.1"),sQuery(id+"F4.wireOp",EDGE,"E20.1.2"),sQuery(id+"F4.wireOp",EDGE,"E20.2.0"),sQuery(id+"F4.wireOp",EDGE,"E20.2.1"),sQuery(id+"F4.wireOp",EDGE,"E20.2.2"),sQuery(id+"F4.wireOp",EDGE,"E21.2.3.0"),sQuery(id+"F4.wireOp",EDGE,"E21.4.3.0"),sQuery(id+"F4.wireOp",EDGE,"E21.8.3.0"),sQuery(id+"F4.wireOp",EDGE,"E22.MirrorCS"),sQuery(id+"F4.wireOp",EDGE,"E23.MirrorCS"),sQuery(id+"F4.wireOp",EDGE,"E24.MirrorCS"),sQuery(id+"F4.wireOp",EDGE,"E25.MirrorCS"),sQuery(id+"F4.wireOp",EDGE,"E26.MirrorCS"),sQuery(id+"F4.wireOp",EDGE,"E27.MirrorCS"),sQuery(id+"F4.wireOp",EDGE,"E30"),sQuery(id+"F4.wireOp",EDGE,"E31"),sQuery(id+"F4.wireOp",EDGE,"E32")])]}),"instanceName":"7"});
            var Q2;
            Q2=makeQuery(id+"F6.opPattern","COPY",BODY,{"derivedFrom":makeQuery(id+"F5.opExtrude","SWEPT_BODY",BODY,{"disambiguationData":[OSD([sQuery(id+"F4.wireOp",EDGE,"E13"),sQuery(id+"F4.wireOp",EDGE,"E17"),sQuery(id+"F4.wireOp",EDGE,"E19.MirrorCS"),sQuery(id+"F4.wireOp",EDGE,"E20.1.0"),sQuery(id+"F4.wireOp",EDGE,"E20.1.1"),sQuery(id+"F4.wireOp",EDGE,"E20.1.2"),sQuery(id+"F4.wireOp",EDGE,"E20.2.0"),sQuery(id+"F4.wireOp",EDGE,"E20.2.1"),sQuery(id+"F4.wireOp",EDGE,"E20.2.2"),sQuery(id+"F4.wireOp",EDGE,"E21.2.3.0"),sQuery(id+"F4.wireOp",EDGE,"E21.4.3.0"),sQuery(id+"F4.wireOp",EDGE,"E21.8.3.0"),sQuery(id+"F4.wireOp",EDGE,"E22.MirrorCS"),sQuery(id+"F4.wireOp",EDGE,"E23.MirrorCS"),sQuery(id+"F4.wireOp",EDGE,"E24.MirrorCS"),sQuery(id+"F4.wireOp",EDGE,"E25.MirrorCS"),sQuery(id+"F4.wireOp",EDGE,"E26.MirrorCS"),sQuery(id+"F4.wireOp",EDGE,"E27.MirrorCS"),sQuery(id+"F4.wireOp",EDGE,"E30"),sQuery(id+"F4.wireOp",EDGE,"E31"),sQuery(id+"F4.wireOp",EDGE,"E32")])]}),"instanceName":"5"});
            var Q3;
            Q3=makeQuery(id+"F6.opPattern","COPY",BODY,{"derivedFrom":makeQuery(id+"F5.opExtrude","SWEPT_BODY",BODY,{"disambiguationData":[OSD([sQuery(id+"F4.wireOp",EDGE,"E13"),sQuery(id+"F4.wireOp",EDGE,"E17"),sQuery(id+"F4.wireOp",EDGE,"E19.MirrorCS"),sQuery(id+"F4.wireOp",EDGE,"E20.1.0"),sQuery(id+"F4.wireOp",EDGE,"E20.1.1"),sQuery(id+"F4.wireOp",EDGE,"E20.1.2"),sQuery(id+"F4.wireOp",EDGE,"E20.2.0"),sQuery(id+"F4.wireOp",EDGE,"E20.2.1"),sQuery(id+"F4.wireOp",EDGE,"E20.2.2"),sQuery(id+"F4.wireOp",EDGE,"E21.2.3.0"),sQuery(id+"F4.wireOp",EDGE,"E21.4.3.0"),sQuery(id+"F4.wireOp",EDGE,"E21.8.3.0"),sQuery(id+"F4.wireOp",EDGE,"E22.MirrorCS"),sQuery(id+"F4.wireOp",EDGE,"E23.MirrorCS"),sQuery(id+"F4.wireOp",EDGE,"E24.MirrorCS"),sQuery(id+"F4.wireOp",EDGE,"E25.MirrorCS"),sQuery(id+"F4.wireOp",EDGE,"E26.MirrorCS"),sQuery(id+"F4.wireOp",EDGE,"E27.MirrorCS"),sQuery(id+"F4.wireOp",EDGE,"E30"),sQuery(id+"F4.wireOp",EDGE,"E31"),sQuery(id+"F4.wireOp",EDGE,"E32")])]}),"instanceName":"6"});
            var Q4;
            Q4=makeQuery(id+"F6.opPattern","COPY",BODY,{"derivedFrom":makeQuery(id+"F5.opExtrude","SWEPT_BODY",BODY,{"disambiguationData":[OSD([sQuery(id+"F4.wireOp",EDGE,"E13"),sQuery(id+"F4.wireOp",EDGE,"E17"),sQuery(id+"F4.wireOp",EDGE,"E19.MirrorCS"),sQuery(id+"F4.wireOp",EDGE,"E20.1.0"),sQuery(id+"F4.wireOp",EDGE,"E20.1.1"),sQuery(id+"F4.wireOp",EDGE,"E20.1.2"),sQuery(id+"F4.wireOp",EDGE,"E20.2.0"),sQuery(id+"F4.wireOp",EDGE,"E20.2.1"),sQuery(id+"F4.wireOp",EDGE,"E20.2.2"),sQuery(id+"F4.wireOp",EDGE,"E21.2.3.0"),sQuery(id+"F4.wireOp",EDGE,"E21.4.3.0"),sQuery(id+"F4.wireOp",EDGE,"E21.8.3.0"),sQuery(id+"F4.wireOp",EDGE,"E22.MirrorCS"),sQuery(id+"F4.wireOp",EDGE,"E23.MirrorCS"),sQuery(id+"F4.wireOp",EDGE,"E24.MirrorCS"),sQuery(id+"F4.wireOp",EDGE,"E25.MirrorCS"),sQuery(id+"F4.wireOp",EDGE,"E26.MirrorCS"),sQuery(id+"F4.wireOp",EDGE,"E27.MirrorCS"),sQuery(id+"F4.wireOp",EDGE,"E30"),sQuery(id+"F4.wireOp",EDGE,"E31"),sQuery(id+"F4.wireOp",EDGE,"E32")])]}),"instanceName":"4"});
            var Q5;
            Q5=makeQuery(id+"F6.opPattern","COPY",BODY,{"derivedFrom":makeQuery(id+"F5.opExtrude","SWEPT_BODY",BODY,{"disambiguationData":[OSD([sQuery(id+"F4.wireOp",EDGE,"E13"),sQuery(id+"F4.wireOp",EDGE,"E17"),sQuery(id+"F4.wireOp",EDGE,"E19.MirrorCS"),sQuery(id+"F4.wireOp",EDGE,"E20.1.0"),sQuery(id+"F4.wireOp",EDGE,"E20.1.1"),sQuery(id+"F4.wireOp",EDGE,"E20.1.2"),sQuery(id+"F4.wireOp",EDGE,"E20.2.0"),sQuery(id+"F4.wireOp",EDGE,"E20.2.1"),sQuery(id+"F4.wireOp",EDGE,"E20.2.2"),sQuery(id+"F4.wireOp",EDGE,"E21.2.3.0"),sQuery(id+"F4.wireOp",EDGE,"E21.4.3.0"),sQuery(id+"F4.wireOp",EDGE,"E21.8.3.0"),sQuery(id+"F4.wireOp",EDGE,"E22.MirrorCS"),sQuery(id+"F4.wireOp",EDGE,"E23.MirrorCS"),sQuery(id+"F4.wireOp",EDGE,"E24.MirrorCS"),sQuery(id+"F4.wireOp",EDGE,"E25.MirrorCS"),sQuery(id+"F4.wireOp",EDGE,"E26.MirrorCS"),sQuery(id+"F4.wireOp",EDGE,"E27.MirrorCS"),sQuery(id+"F4.wireOp",EDGE,"E30"),sQuery(id+"F4.wireOp",EDGE,"E31"),sQuery(id+"F4.wireOp",EDGE,"E32")])]}),"instanceName":"3"});
            var Q6;
            Q6=makeQuery(id+"F6.opPattern","COPY",BODY,{"derivedFrom":makeQuery(id+"F5.opExtrude","SWEPT_BODY",BODY,{"disambiguationData":[OSD([sQuery(id+"F4.wireOp",EDGE,"E13"),sQuery(id+"F4.wireOp",EDGE,"E17"),sQuery(id+"F4.wireOp",EDGE,"E19.MirrorCS"),sQuery(id+"F4.wireOp",EDGE,"E20.1.0"),sQuery(id+"F4.wireOp",EDGE,"E20.1.1"),sQuery(id+"F4.wireOp",EDGE,"E20.1.2"),sQuery(id+"F4.wireOp",EDGE,"E20.2.0"),sQuery(id+"F4.wireOp",EDGE,"E20.2.1"),sQuery(id+"F4.wireOp",EDGE,"E20.2.2"),sQuery(id+"F4.wireOp",EDGE,"E21.2.3.0"),sQuery(id+"F4.wireOp",EDGE,"E21.4.3.0"),sQuery(id+"F4.wireOp",EDGE,"E21.8.3.0"),sQuery(id+"F4.wireOp",EDGE,"E22.MirrorCS"),sQuery(id+"F4.wireOp",EDGE,"E23.MirrorCS"),sQuery(id+"F4.wireOp",EDGE,"E24.MirrorCS"),sQuery(id+"F4.wireOp",EDGE,"E25.MirrorCS"),sQuery(id+"F4.wireOp",EDGE,"E26.MirrorCS"),sQuery(id+"F4.wireOp",EDGE,"E27.MirrorCS"),sQuery(id+"F4.wireOp",EDGE,"E30"),sQuery(id+"F4.wireOp",EDGE,"E31"),sQuery(id+"F4.wireOp",EDGE,"E32")])]}),"instanceName":"2"});
            var Q7;
            Q7=makeQuery(id+"F6.opPattern","COPY",BODY,{"derivedFrom":makeQuery(id+"F5.opExtrude","SWEPT_BODY",BODY,{"disambiguationData":[OSD([sQuery(id+"F4.wireOp",EDGE,"E13"),sQuery(id+"F4.wireOp",EDGE,"E17"),sQuery(id+"F4.wireOp",EDGE,"E19.MirrorCS"),sQuery(id+"F4.wireOp",EDGE,"E20.1.0"),sQuery(id+"F4.wireOp",EDGE,"E20.1.1"),sQuery(id+"F4.wireOp",EDGE,"E20.1.2"),sQuery(id+"F4.wireOp",EDGE,"E20.2.0"),sQuery(id+"F4.wireOp",EDGE,"E20.2.1"),sQuery(id+"F4.wireOp",EDGE,"E20.2.2"),sQuery(id+"F4.wireOp",EDGE,"E21.2.3.0"),sQuery(id+"F4.wireOp",EDGE,"E21.4.3.0"),sQuery(id+"F4.wireOp",EDGE,"E21.8.3.0"),sQuery(id+"F4.wireOp",EDGE,"E22.MirrorCS"),sQuery(id+"F4.wireOp",EDGE,"E23.MirrorCS"),sQuery(id+"F4.wireOp",EDGE,"E24.MirrorCS"),sQuery(id+"F4.wireOp",EDGE,"E25.MirrorCS"),sQuery(id+"F4.wireOp",EDGE,"E26.MirrorCS"),sQuery(id+"F4.wireOp",EDGE,"E27.MirrorCS"),sQuery(id+"F4.wireOp",EDGE,"E30"),sQuery(id+"F4.wireOp",EDGE,"E31"),sQuery(id+"F4.wireOp",EDGE,"E32")])]}),"instanceName":"1"});
            var Q8;
            Q8=makeQuery(id+"F5.opExtrude","SWEPT_BODY",BODY,{"disambiguationData":[OSD([sQuery(id+"F4.wireOp",EDGE,"E13"),sQuery(id+"F4.wireOp",EDGE,"E17"),sQuery(id+"F4.wireOp",EDGE,"E19.MirrorCS"),sQuery(id+"F4.wireOp",EDGE,"E20.1.0"),sQuery(id+"F4.wireOp",EDGE,"E20.1.1"),sQuery(id+"F4.wireOp",EDGE,"E20.1.2"),sQuery(id+"F4.wireOp",EDGE,"E20.2.0"),sQuery(id+"F4.wireOp",EDGE,"E20.2.1"),sQuery(id+"F4.wireOp",EDGE,"E20.2.2"),sQuery(id+"F4.wireOp",EDGE,"E21.2.3.0"),sQuery(id+"F4.wireOp",EDGE,"E21.4.3.0"),sQuery(id+"F4.wireOp",EDGE,"E21.8.3.0"),sQuery(id+"F4.wireOp",EDGE,"E22.MirrorCS"),sQuery(id+"F4.wireOp",EDGE,"E23.MirrorCS"),sQuery(id+"F4.wireOp",EDGE,"E24.MirrorCS"),sQuery(id+"F4.wireOp",EDGE,"E25.MirrorCS"),sQuery(id+"F4.wireOp",EDGE,"E26.MirrorCS"),sQuery(id+"F4.wireOp",EDGE,"E27.MirrorCS"),sQuery(id+"F4.wireOp",EDGE,"E30"),sQuery(id+"F4.wireOp",EDGE,"E31"),sQuery(id+"F4.wireOp",EDGE,"E32")])]});
            var Q9;
            Q9=makeQuery(id+"F1.opExtrude","SWEPT_BODY",BODY,{"disambiguationData":[OSD([sQuery(id+"F0.wireOp",EDGE,"E1"),sQuery(id+"F0.wireOp",EDGE,"E3"),sQuery(id+"F0.wireOp",EDGE,"E6.1.0"),sQuery(id+"F0.wireOp",EDGE,"E6.1.1"),sQuery(id+"F0.wireOp",EDGE,"E6.2.0"),sQuery(id+"F0.wireOp",EDGE,"E6.2.1"),sQuery(id+"F0.wireOp",EDGE,"E7.3.3.0"),sQuery(id+"F0.wireOp",EDGE,"E7.4.3.0"),sQuery(id+"F0.wireOp",EDGE,"E7.3.4.0"),sQuery(id+"F0.wireOp",EDGE,"E7.4.4.0"),sQuery(id+"F0.wireOp",EDGE,"E7.3.5.0"),sQuery(id+"F0.wireOp",EDGE,"E7.4.5.0"),sQuery(id+"F0.wireOp",EDGE,"E7.3.6.0"),sQuery(id+"F0.wireOp",EDGE,"E7.4.6.0"),sQuery(id+"F0.wireOp",EDGE,"E7.3.7.0"),sQuery(id+"F0.wireOp",EDGE,"E7.4.7.0"),sQuery(id+"F0.wireOp",EDGE,"E7.3.8.0"),sQuery(id+"F0.wireOp",EDGE,"E7.4.8.0"),sQuery(id+"F0.wireOp",EDGE,"E7.3.9.0"),sQuery(id+"F0.wireOp",EDGE,"E7.4.9.0"),sQuery(id+"F0.wireOp",EDGE,"E7.3.10.0"),sQuery(id+"F0.wireOp",EDGE,"E7.4.10.0"),sQuery(id+"F0.wireOp",EDGE,"E7.3.11.0"),sQuery(id+"F0.wireOp",EDGE,"E7.4.11.0"),sQuery(id+"F0.wireOp",EDGE,"E7.3.12.0"),sQuery(id+"F0.wireOp",EDGE,"E7.4.12.0"),sQuery(id+"F0.wireOp",EDGE,"E7.3.13.0"),sQuery(id+"F0.wireOp",EDGE,"E7.4.13.0"),sQuery(id+"F0.wireOp",EDGE,"E7.3.14.0"),sQuery(id+"F0.wireOp",EDGE,"E7.4.14.0"),sQuery(id+"F0.wireOp",EDGE,"E7.3.15.0"),sQuery(id+"F0.wireOp",EDGE,"E7.4.15.0"),sQuery(id+"F0.wireOp",EDGE,"E7.3.16.0"),sQuery(id+"F0.wireOp",EDGE,"E7.4.16.0"),sQuery(id+"F0.wireOp",EDGE,"E7.3.17.0"),sQuery(id+"F0.wireOp",EDGE,"E7.4.17.0"),sQuery(id+"F0.wireOp",EDGE,"E7.3.18.0"),sQuery(id+"F0.wireOp",EDGE,"E7.4.18.0"),sQuery(id+"F0.wireOp",EDGE,"E7.3.19.0"),sQuery(id+"F0.wireOp",EDGE,"E7.4.19.0"),sQuery(id+"F0.wireOp",EDGE,"E7.3.20.0"),sQuery(id+"F0.wireOp",EDGE,"E7.4.20.0"),sQuery(id+"F0.wireOp",EDGE,"E7.3.21.0"),sQuery(id+"F0.wireOp",EDGE,"E7.4.21.0"),sQuery(id+"F0.wireOp",EDGE,"E7.3.22.0"),sQuery(id+"F0.wireOp",EDGE,"E7.4.22.0"),sQuery(id+"F0.wireOp",EDGE,"E7.3.23.0"),sQuery(id+"F0.wireOp",EDGE,"E7.4.23.0"),sQuery(id+"F0.wireOp",EDGE,"E7.3.24.0"),sQuery(id+"F0.wireOp",EDGE,"E7.4.24.0"),sQuery(id+"F0.wireOp",EDGE,"E7.3.25.0"),sQuery(id+"F0.wireOp",EDGE,"E7.4.25.0"),sQuery(id+"F0.wireOp",EDGE,"E7.3.26.0"),sQuery(id+"F0.wireOp",EDGE,"E7.4.26.0"),sQuery(id+"F0.wireOp",EDGE,"E7.3.27.0"),sQuery(id+"F0.wireOp",EDGE,"E7.4.27.0"),sQuery(id+"F0.wireOp",EDGE,"E7.3.28.0"),sQuery(id+"F0.wireOp",EDGE,"E7.4.28.0"),sQuery(id+"F0.wireOp",EDGE,"E7.3.29.0"),sQuery(id+"F0.wireOp",EDGE,"E7.4.29.0"),sQuery(id+"F0.wireOp",EDGE,"E7.3.30.0"),sQuery(id+"F0.wireOp",EDGE,"E7.4.30.0"),sQuery(id+"F0.wireOp",EDGE,"E7.3.31.0"),sQuery(id+"F0.wireOp",EDGE,"E7.4.31.0"),sQuery(id+"F0.wireOp",EDGE,"E7.3.32.0"),sQuery(id+"F0.wireOp",EDGE,"E7.4.32.0"),sQuery(id+"F0.wireOp",EDGE,"E7.3.33.0"),sQuery(id+"F0.wireOp",EDGE,"E7.4.33.0"),sQuery(id+"F0.wireOp",EDGE,"E7.3.34.0"),sQuery(id+"F0.wireOp",EDGE,"E7.4.34.0"),sQuery(id+"F0.wireOp",EDGE,"E7.3.35.0"),sQuery(id+"F0.wireOp",EDGE,"E7.4.35.0"),sQuery(id+"F0.wireOp",EDGE,"E7.3.36.0"),sQuery(id+"F0.wireOp",EDGE,"E7.4.36.0"),sQuery(id+"F0.wireOp",EDGE,"E7.3.37.0"),sQuery(id+"F0.wireOp",EDGE,"E7.4.37.0"),sQuery(id+"F0.wireOp",EDGE,"E7.3.38.0"),sQuery(id+"F0.wireOp",EDGE,"E7.4.38.0"),sQuery(id+"F0.wireOp",EDGE,"E7.3.39.0"),sQuery(id+"F0.wireOp",EDGE,"E7.4.39.0"),sQuery(id+"F0.wireOp",EDGE,"E7.3.40.0"),sQuery(id+"F0.wireOp",EDGE,"E7.4.40.0"),sQuery(id+"F0.wireOp",EDGE,"E7.3.41.0"),sQuery(id+"F0.wireOp",EDGE,"E7.4.41.0"),sQuery(id+"F0.wireOp",EDGE,"E7.3.42.0"),sQuery(id+"F0.wireOp",EDGE,"E7.4.42.0"),sQuery(id+"F0.wireOp",EDGE,"E7.3.43.0"),sQuery(id+"F0.wireOp",EDGE,"E7.4.43.0"),sQuery(id+"F0.wireOp",EDGE,"E7.3.44.0"),sQuery(id+"F0.wireOp",EDGE,"E7.4.44.0"),sQuery(id+"F0.wireOp",EDGE,"E7.3.45.0"),sQuery(id+"F0.wireOp",EDGE,"E7.4.45.0"),sQuery(id+"F0.wireOp",EDGE,"E7.3.46.0"),sQuery(id+"F0.wireOp",EDGE,"E7.4.46.0"),sQuery(id+"F0.wireOp",EDGE,"E7.3.47.0"),sQuery(id+"F0.wireOp",EDGE,"E7.4.47.0"),sQuery(id+"F0.wireOp",EDGE,"E7.3.48.0"),sQuery(id+"F0.wireOp",EDGE,"E7.4.48.0"),sQuery(id+"F0.wireOp",EDGE,"E7.3.49.0"),sQuery(id+"F0.wireOp",EDGE,"E7.4.49.0")])]});
            var Q10;
            Q10=makeQuery(id+"F15.opPattern","COPY",BODY,{"derivedFrom":makeQuery(id+"F13.opExtrude","SWEPT_BODY",BODY,{"disambiguationData":[OSD([sQuery(id+"F11.wireOp",EDGE,"E53"),sQuery(id+"F11.wireOp",EDGE,"E54"),sQuery(id+"F11.wireOp",EDGE,"E55"),sQuery(id+"F11.wireOp",EDGE,"E56"),sQuery(id+"F11.wireOp",EDGE,"E57")])]}),"instanceName":"2"});
            var Q11;
            Q11=makeQuery(id+"F15.opPattern","COPY",BODY,{"derivedFrom":makeQuery(id+"F12.opExtrude","SWEPT_BODY",BODY,{"disambiguationData":[OSD([sQuery(id+"F11.wireOp",EDGE,"E52"),sQuery(id+"F11.wireOp",EDGE,"E53"),sQuery(id+"F11.wireOp",EDGE,"E55"),sQuery(id+"F11.wireOp",EDGE,"E56"),sQuery(id+"F11.wireOp",EDGE,"E57")])]}),"instanceName":"2"});
            var Q12;
            Q12=makeQuery(id+"F15.opPattern","COPY",BODY,{"derivedFrom":makeQuery(id+"F13.opExtrude","SWEPT_BODY",BODY,{"disambiguationData":[OSD([sQuery(id+"F11.wireOp",EDGE,"E53"),sQuery(id+"F11.wireOp",EDGE,"E54"),sQuery(id+"F11.wireOp",EDGE,"E55"),sQuery(id+"F11.wireOp",EDGE,"E56"),sQuery(id+"F11.wireOp",EDGE,"E57")])]}),"instanceName":"1"});
            var Q13;
            Q13=makeQuery(id+"F14.opExtrude","SWEPT_BODY",BODY,{"disambiguationData":[OSD([sQuery(id+"F11.wireOp",EDGE,"E57")])]});
            var Q14;
            Q14=makeQuery(id+"F15.opPattern","COPY",BODY,{"derivedFrom":makeQuery(id+"F12.opExtrude","SWEPT_BODY",BODY,{"disambiguationData":[OSD([sQuery(id+"F11.wireOp",EDGE,"E52"),sQuery(id+"F11.wireOp",EDGE,"E53"),sQuery(id+"F11.wireOp",EDGE,"E55"),sQuery(id+"F11.wireOp",EDGE,"E56"),sQuery(id+"F11.wireOp",EDGE,"E57")])]}),"instanceName":"1"});
            var Q15;
            Q15=makeQuery(id+"F12.opExtrude","SWEPT_BODY",BODY,{"disambiguationData":[OSD([sQuery(id+"F11.wireOp",EDGE,"E52"),sQuery(id+"F11.wireOp",EDGE,"E53"),sQuery(id+"F11.wireOp",EDGE,"E55"),sQuery(id+"F11.wireOp",EDGE,"E56"),sQuery(id+"F11.wireOp",EDGE,"E57")])]});
            var Q16;
            Q16=makeQuery(id+"F13.opExtrude","SWEPT_BODY",BODY,{"disambiguationData":[OSD([sQuery(id+"F11.wireOp",EDGE,"E53"),sQuery(id+"F11.wireOp",EDGE,"E54"),sQuery(id+"F11.wireOp",EDGE,"E55"),sQuery(id+"F11.wireOp",EDGE,"E56"),sQuery(id+"F11.wireOp",EDGE,"E57")])]});
            var Q17;
            Q17=makeQuery(id+"F15.opPattern","COPY",BODY,{"derivedFrom":makeQuery(id+"F13.opExtrude","SWEPT_BODY",BODY,{"disambiguationData":[OSD([sQuery(id+"F11.wireOp",EDGE,"E53"),sQuery(id+"F11.wireOp",EDGE,"E54"),sQuery(id+"F11.wireOp",EDGE,"E55"),sQuery(id+"F11.wireOp",EDGE,"E56"),sQuery(id+"F11.wireOp",EDGE,"E57")])]}),"instanceName":"5"});
            var Q18;
            Q18=makeQuery(id+"F15.opPattern","COPY",BODY,{"derivedFrom":makeQuery(id+"F12.opExtrude","SWEPT_BODY",BODY,{"disambiguationData":[OSD([sQuery(id+"F11.wireOp",EDGE,"E52"),sQuery(id+"F11.wireOp",EDGE,"E53"),sQuery(id+"F11.wireOp",EDGE,"E55"),sQuery(id+"F11.wireOp",EDGE,"E56"),sQuery(id+"F11.wireOp",EDGE,"E57")])]}),"instanceName":"5"});
            var Q19;
            Q19=makeQuery(id+"F15.opPattern","COPY",BODY,{"derivedFrom":makeQuery(id+"F13.opExtrude","SWEPT_BODY",BODY,{"disambiguationData":[OSD([sQuery(id+"F11.wireOp",EDGE,"E53"),sQuery(id+"F11.wireOp",EDGE,"E54"),sQuery(id+"F11.wireOp",EDGE,"E55"),sQuery(id+"F11.wireOp",EDGE,"E56"),sQuery(id+"F11.wireOp",EDGE,"E57")])]}),"instanceName":"3"});
            var Q20;
            Q20=makeQuery(id+"F15.opPattern","COPY",BODY,{"derivedFrom":makeQuery(id+"F12.opExtrude","SWEPT_BODY",BODY,{"disambiguationData":[OSD([sQuery(id+"F11.wireOp",EDGE,"E52"),sQuery(id+"F11.wireOp",EDGE,"E53"),sQuery(id+"F11.wireOp",EDGE,"E55"),sQuery(id+"F11.wireOp",EDGE,"E56"),sQuery(id+"F11.wireOp",EDGE,"E57")])]}),"instanceName":"3"});
            var Q21;
            Q21=makeQuery(id+"F15.opPattern","COPY",BODY,{"derivedFrom":makeQuery(id+"F14.opExtrude","SWEPT_BODY",BODY,{"disambiguationData":[OSD([sQuery(id+"F11.wireOp",EDGE,"E57")])]}),"instanceName":"4"});
            var Q22;
            Q22=makeQuery(id+"F15.opPattern","COPY",BODY,{"derivedFrom":makeQuery(id+"F12.opExtrude","SWEPT_BODY",BODY,{"disambiguationData":[OSD([sQuery(id+"F11.wireOp",EDGE,"E52"),sQuery(id+"F11.wireOp",EDGE,"E53"),sQuery(id+"F11.wireOp",EDGE,"E55"),sQuery(id+"F11.wireOp",EDGE,"E56"),sQuery(id+"F11.wireOp",EDGE,"E57")])]}),"instanceName":"6"});
            var Q23;
            Q23=makeQuery(id+"F15.opPattern","COPY",BODY,{"derivedFrom":makeQuery(id+"F14.opExtrude","SWEPT_BODY",BODY,{"disambiguationData":[OSD([sQuery(id+"F11.wireOp",EDGE,"E57")])]}),"instanceName":"2"});
            var Q24;
            Q24=makeQuery(id+"F15.opPattern","COPY",BODY,{"derivedFrom":makeQuery(id+"F12.opExtrude","SWEPT_BODY",BODY,{"disambiguationData":[OSD([sQuery(id+"F11.wireOp",EDGE,"E52"),sQuery(id+"F11.wireOp",EDGE,"E53"),sQuery(id+"F11.wireOp",EDGE,"E55"),sQuery(id+"F11.wireOp",EDGE,"E56"),sQuery(id+"F11.wireOp",EDGE,"E57")])]}),"instanceName":"4"});
            var Q25;
            Q25=makeQuery(id+"F15.opPattern","COPY",BODY,{"derivedFrom":makeQuery(id+"F13.opExtrude","SWEPT_BODY",BODY,{"disambiguationData":[OSD([sQuery(id+"F11.wireOp",EDGE,"E53"),sQuery(id+"F11.wireOp",EDGE,"E54"),sQuery(id+"F11.wireOp",EDGE,"E55"),sQuery(id+"F11.wireOp",EDGE,"E56"),sQuery(id+"F11.wireOp",EDGE,"E57")])]}),"instanceName":"7"});
            var Q26;
            Q26=makeQuery(id+"F15.opPattern","COPY",BODY,{"derivedFrom":makeQuery(id+"F12.opExtrude","SWEPT_BODY",BODY,{"disambiguationData":[OSD([sQuery(id+"F11.wireOp",EDGE,"E52"),sQuery(id+"F11.wireOp",EDGE,"E53"),sQuery(id+"F11.wireOp",EDGE,"E55"),sQuery(id+"F11.wireOp",EDGE,"E56"),sQuery(id+"F11.wireOp",EDGE,"E57")])]}),"instanceName":"7"});
            var Q27;
            Q27=makeQuery(id+"F15.opPattern","COPY",BODY,{"derivedFrom":makeQuery(id+"F13.opExtrude","SWEPT_BODY",BODY,{"disambiguationData":[OSD([sQuery(id+"F11.wireOp",EDGE,"E53"),sQuery(id+"F11.wireOp",EDGE,"E54"),sQuery(id+"F11.wireOp",EDGE,"E55"),sQuery(id+"F11.wireOp",EDGE,"E56"),sQuery(id+"F11.wireOp",EDGE,"E57")])]}),"instanceName":"6"});
            var Q28;
            Q28=makeQuery(id+"F15.opPattern","COPY",BODY,{"derivedFrom":makeQuery(id+"F14.opExtrude","SWEPT_BODY",BODY,{"disambiguationData":[OSD([sQuery(id+"F11.wireOp",EDGE,"E57")])]}),"instanceName":"1"});
            var Q29;
            Q29=makeQuery(id+"F15.opPattern","COPY",BODY,{"derivedFrom":makeQuery(id+"F14.opExtrude","SWEPT_BODY",BODY,{"disambiguationData":[OSD([sQuery(id+"F11.wireOp",EDGE,"E57")])]}),"instanceName":"5"});
            var Q30;
            Q30=makeQuery(id+"F15.opPattern","COPY",BODY,{"derivedFrom":makeQuery(id+"F14.opExtrude","SWEPT_BODY",BODY,{"disambiguationData":[OSD([sQuery(id+"F11.wireOp",EDGE,"E57")])]}),"instanceName":"3"});
            var Q31;
            Q31=makeQuery(id+"F15.opPattern","COPY",BODY,{"derivedFrom":makeQuery(id+"F14.opExtrude","SWEPT_BODY",BODY,{"disambiguationData":[OSD([sQuery(id+"F11.wireOp",EDGE,"E57")])]}),"instanceName":"7"});
            var Q32;
            Q32=makeQuery(id+"F15.opPattern","COPY",BODY,{"derivedFrom":makeQuery(id+"F14.opExtrude","SWEPT_BODY",BODY,{"disambiguationData":[OSD([sQuery(id+"F11.wireOp",EDGE,"E57")])]}),"instanceName":"6"});
            var Q33;
            Q33=sQuery(id+"F2.wireOp",EDGE,"E11");
            transform(context, id + "F27", {"entities" : qUnion([Q0, Q1, Q2, Q3, Q4, Q5, Q6, Q7, Q8, Q9, Q10, Q11, Q12, Q13, Q14, Q15, Q16, Q17, Q18, Q19, Q20, Q21, Q22, Q23, Q24, Q25, Q26, Q27, Q28, Q29, Q30, Q31, Q32]), "transformType" : TransformType.ROTATION, "transformAxis" : qUnion([Q33]), "angle" : 3.6 * degree, "makeCopy" : false});
        }
        {
            var Q0;
            Q0=makeQuery(id+"F20.opPattern","COPY",BODY,{"derivedFrom":makeQuery(id+"F18.opExtrude","SWEPT_BODY",BODY,{"disambiguationData":[OSD([sQuery(id+"F16.wireOp",EDGE,"E58.top"),sQuery(id+"F16.wireOp",EDGE,"E58.left"),sQuery(id+"F16.wireOp",EDGE,"E58.right"),sQuery(id+"F16.wireOp",EDGE,"E60"),sQuery(id+"F16.wireOp",EDGE,"E61")])]}),"instanceName":"1"});
            var Q1;
            Q1=makeQuery(id+"F20.opPattern","COPY",BODY,{"derivedFrom":makeQuery(id+"F17.opExtrude","SWEPT_BODY",BODY,{"disambiguationData":[OSD([sQuery(id+"F16.wireOp",EDGE,"E58.bottom"),sQuery(id+"F16.wireOp",EDGE,"E58.left"),sQuery(id+"F16.wireOp",EDGE,"E58.right"),sQuery(id+"F16.wireOp",EDGE,"E60"),sQuery(id+"F16.wireOp",EDGE,"E61")])]}),"instanceName":"1"});
            var Q2;
            Q2=makeQuery(id+"F20.opPattern","COPY",FACE,{"derivedFrom":makeQuery(id+"F18.opExtrude","SWEPT_FACE",FACE,{"disambiguationData":[OSD([sQuery(id+"F16.wireOp",EDGE,"E61")])]}),"instanceName":"1"});
            transform(context, id + "F28", {"entities" : qUnion([Q0, Q1]), "transformType" : TransformType.ROTATION, "transformAxis" : qUnion([Q2]), "angle" : 180 * degree, "makeCopy" : false});
        }
        {
            var Q0;
            Q0=makeQuery(id+"F17.opExtrude","SWEPT_BODY",BODY,{"disambiguationData":[OSD([sQuery(id+"F16.wireOp",EDGE,"E58.bottom"),sQuery(id+"F16.wireOp",EDGE,"E58.left"),sQuery(id+"F16.wireOp",EDGE,"E58.right"),sQuery(id+"F16.wireOp",EDGE,"E60"),sQuery(id+"F16.wireOp",EDGE,"E61")])]});
            var Q1;
            Q1=makeQuery(id+"F18.opExtrude","SWEPT_BODY",BODY,{"disambiguationData":[OSD([sQuery(id+"F16.wireOp",EDGE,"E58.top"),sQuery(id+"F16.wireOp",EDGE,"E58.left"),sQuery(id+"F16.wireOp",EDGE,"E58.right"),sQuery(id+"F16.wireOp",EDGE,"E60"),sQuery(id+"F16.wireOp",EDGE,"E61")])]});
            var Q2;
            Q2=makeQuery(id+"F18.opExtrude","SWEPT_FACE",FACE,{"disambiguationData":[OSD([sQuery(id+"F16.wireOp",EDGE,"E61")])]});
            transform(context, id + "F29", {"entities" : qUnion([Q0, Q1]), "transformType" : TransformType.ROTATION, "transformAxis" : qUnion([Q2]), "angle" : 90 * degree, "makeCopy" : false});
        }
        {
            var Q0;
            Q0=makeQuery(id+"F20.opPattern","COPY",BODY,{"derivedFrom":makeQuery(id+"F18.opExtrude","SWEPT_BODY",BODY,{"disambiguationData":[OSD([sQuery(id+"F16.wireOp",EDGE,"E58.top"),sQuery(id+"F16.wireOp",EDGE,"E58.left"),sQuery(id+"F16.wireOp",EDGE,"E58.right"),sQuery(id+"F16.wireOp",EDGE,"E60"),sQuery(id+"F16.wireOp",EDGE,"E61")])]}),"instanceName":"2"});
            var Q1;
            Q1=makeQuery(id+"F20.opPattern","COPY",BODY,{"derivedFrom":makeQuery(id+"F17.opExtrude","SWEPT_BODY",BODY,{"disambiguationData":[OSD([sQuery(id+"F16.wireOp",EDGE,"E58.bottom"),sQuery(id+"F16.wireOp",EDGE,"E58.left"),sQuery(id+"F16.wireOp",EDGE,"E58.right"),sQuery(id+"F16.wireOp",EDGE,"E60"),sQuery(id+"F16.wireOp",EDGE,"E61")])]}),"instanceName":"2"});
            var Q2;
            Q2=makeQuery(id+"F20.opPattern","COPY",FACE,{"derivedFrom":makeQuery(id+"F17.opExtrude","SWEPT_FACE",FACE,{"disambiguationData":[OSD([sQuery(id+"F16.wireOp",EDGE,"E61")])]}),"instanceName":"2"});
            transform(context, id + "F30", {"entities" : qUnion([Q0, Q1]), "transformType" : TransformType.ROTATION, "transformAxis" : qUnion([Q2]), "angle" : 90 * degree, "makeCopy" : false});
        }
        {
            var Q0;
            Q0=makeQuery(id+"F15.opPattern","COPY",BODY,{"derivedFrom":makeQuery(id+"F12.opExtrude","SWEPT_BODY",BODY,{"disambiguationData":[OSD([sQuery(id+"F11.wireOp",EDGE,"E52"),sQuery(id+"F11.wireOp",EDGE,"E53"),sQuery(id+"F11.wireOp",EDGE,"E55"),sQuery(id+"F11.wireOp",EDGE,"E56"),sQuery(id+"F11.wireOp",EDGE,"E57")])]}),"instanceName":"5"});
            var Q1;
            Q1=makeQuery(id+"F15.opPattern","COPY",BODY,{"derivedFrom":makeQuery(id+"F13.opExtrude","SWEPT_BODY",BODY,{"disambiguationData":[OSD([sQuery(id+"F11.wireOp",EDGE,"E53"),sQuery(id+"F11.wireOp",EDGE,"E54"),sQuery(id+"F11.wireOp",EDGE,"E55"),sQuery(id+"F11.wireOp",EDGE,"E56"),sQuery(id+"F11.wireOp",EDGE,"E57")])]}),"instanceName":"5"});
            var Q2;
            Q2=makeQuery(id+"F15.opPattern","COPY",EDGE,{"derivedFrom":makeQuery(id+"F14.opExtrude","CAP_EDGE",EDGE,{"disambiguationData":[OSD([sQuery(id+"F11.wireOp",EDGE,"E57")])],"isStart":true}),"instanceName":"5"});
            transform(context, id + "F31", {"entities" : qUnion([Q0, Q1]), "transformType" : TransformType.ROTATION, "transformAxis" : qUnion([Q2]), "angle" : 180 * degree, "makeCopy" : false});
        }
        {
            var Q0;
            Q0=makeQuery(id+"F15.opPattern","COPY",BODY,{"derivedFrom":makeQuery(id+"F13.opExtrude","SWEPT_BODY",BODY,{"disambiguationData":[OSD([sQuery(id+"F11.wireOp",EDGE,"E53"),sQuery(id+"F11.wireOp",EDGE,"E54"),sQuery(id+"F11.wireOp",EDGE,"E55"),sQuery(id+"F11.wireOp",EDGE,"E56"),sQuery(id+"F11.wireOp",EDGE,"E57")])]}),"instanceName":"1"});
            var Q1;
            Q1=makeQuery(id+"F15.opPattern","COPY",BODY,{"derivedFrom":makeQuery(id+"F12.opExtrude","SWEPT_BODY",BODY,{"disambiguationData":[OSD([sQuery(id+"F11.wireOp",EDGE,"E52"),sQuery(id+"F11.wireOp",EDGE,"E53"),sQuery(id+"F11.wireOp",EDGE,"E55"),sQuery(id+"F11.wireOp",EDGE,"E56"),sQuery(id+"F11.wireOp",EDGE,"E57")])]}),"instanceName":"1"});
            var Q2;
            Q2=makeQuery(id+"F15.opPattern","COPY",EDGE,{"derivedFrom":makeQuery(id+"F14.opExtrude","CAP_EDGE",EDGE,{"disambiguationData":[OSD([sQuery(id+"F11.wireOp",EDGE,"E57")])],"isStart":true}),"instanceName":"1"});
            transform(context, id + "F32", {"entities" : qUnion([Q0, Q1]), "transformType" : TransformType.ROTATION, "transformAxis" : qUnion([Q2]), "angle" : 180 * degree, "makeCopy" : false});
        }
    });
